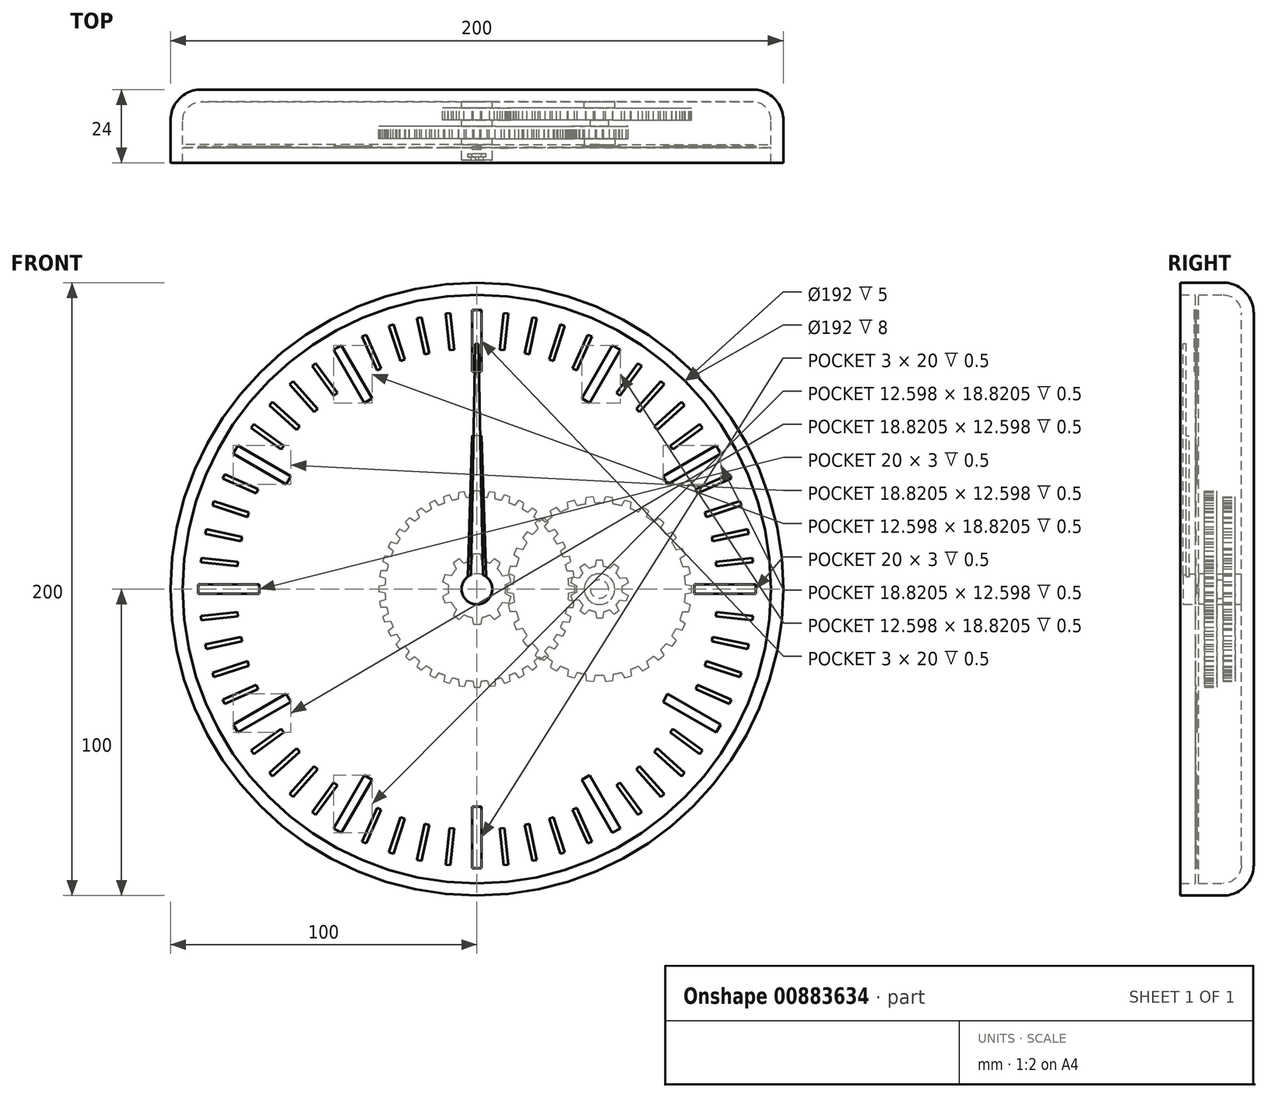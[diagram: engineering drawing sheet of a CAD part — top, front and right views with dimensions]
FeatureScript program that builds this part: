
annotation { "Feature Type Name" : "Feature", "Feature Type Description" : "" }
export const myFeature = defineFeature(function(context is Context, id is Id, definition is map)
    precondition{}
    {
        {
            var Q0;
            Q0=qCreatedBy(makeId("Front.planeOp"),FACE);
            var sketch = newSketch(context, id + "F0", { "sketchPlane" : qUnion([Q0])});
            skCircle(sketch, "E0", {"center": v(0, 0) * mm, "radius": 100 * mm});
            skSolve(sketch);
        }
        {
            var Q0;
            Q0=makeQuery(id+"F0.imprint","IMPRINT",FACE,{"disambiguationData":[TD([[makeQuery(id+"F0.imprint","IMPRINT",EDGE,{"derivedFrom":sQuery(id+"F0.wireOp",EDGE,"E0")}),1.0]])]});
            extrude(context, id + "F1", {"entities" : qUnion([Q0]), "depth" : 24 * mm, "offsetDistance" : 25 * mm});
        }
        {
            var Q0;
            Q0=makeQuery(id+"F1.opExtrude","CAP_EDGE",EDGE,{"disambiguationData":[OSD([sQuery(id+"F0.wireOp",EDGE,"E0")])],"isStart":true});
            fillet(context, id + "F2", {"entities" : qUnion([Q0]), "radius" : 10 * mm, "tangentPropagation" : true, "allowEdgeOverflow" : false});
        }
        {
            var Q0;
            Q0=makeQuery(id+"F1.opExtrude","CAP_FACE",FACE,{"disambiguationData":[OSD([sQuery(id+"F0.wireOp",EDGE,"E0")])],"isStart":false});
            shell(context, id + "F3", {"entities" : qUnion([Q0]), "thickness" : 4 * mm});
        }
        {
            var Q0;
            {var subQ0=sQuery(id+"F0.wireOp",EDGE,"E0");Q0=makeQuery(id+"F3.opShell","OFFSET_FACE",FACE,{"disambiguationData":[OSD([subQ0]),TDD([makeQuery(id+"F1.opExtrude","CAP_FACE",FACE,{"disambiguationData":[OSD([subQ0])],"isStart":true})])]});}
            var sketch = newSketch(context, id + "F4", { "sketchPlane" : qUnion([Q0])});
            skCircle(sketch, "E1", {"center": v(0, 0) * mm, "radius": 3 * mm});
            skCircle(sketch, "E2", {"center": v(0, 0) * mm, "radius": 5 * mm});
            skCircle(sketch, "E3", {"center": v(40, 0) * mm, "radius": 3 * mm});
            skCircle(sketch, "E4", {"center": v(40, 0) * mm, "radius": 5 * mm});
            skSolve(sketch);
        }
        {
            var Q0;
            Q0=makeQuery(id+"F4.imprint","IMPRINT",FACE,{"disambiguationData":[TD([[makeQuery(id+"F4.imprint","IMPRINT",EDGE,{"derivedFrom":sQuery(id+"F4.wireOp",EDGE,"E1")}),-1.0]])]});
            var Q1;
            Q1=makeQuery(id+"F4.imprint","IMPRINT",FACE,{"disambiguationData":[TD([[makeQuery(id+"F4.imprint","IMPRINT",EDGE,{"derivedFrom":sQuery(id+"F4.wireOp",EDGE,"E3")}),-1.0]])]});
            extrude(context, id + "F5", {"entities" : qUnion([Q0, Q1]), "operationType" : NewBodyOperationType.ADD, "depth" : 2 * mm, "offsetDistance" : 25 * mm});
        }
        {
            var Q0;
            Q0=makeQuery(id+"F4.imprint","IMPRINT",FACE,{"disambiguationData":[TD([[makeQuery(id+"F4.imprint","IMPRINT",EDGE,{"derivedFrom":sQuery(id+"F4.wireOp",EDGE,"E1")}),1.0]])]});
            extrude(context, id + "F6", {"entities" : qUnion([Q0]), "depth" : 19 * mm, "offsetDistance" : 25 * mm});
        }
        {
            var Q0;
            Q0=makeQuery(id+"F4.imprint","IMPRINT",FACE,{"disambiguationData":[TD([[makeQuery(id+"F4.imprint","IMPRINT",EDGE,{"derivedFrom":sQuery(id+"F4.wireOp",EDGE,"E3")}),1.0]])]});
            extrude(context, id + "F7", {"entities" : qUnion([Q0]), "depth" : 8 * mm, "offsetDistance" : 25 * mm});
        }
        {
            var Q0;
            Q0=makeQuery(id+"F5.opExtrude","CAP_FACE",FACE,{"disambiguationData":[OSD([sQuery(id+"F4.wireOp",EDGE,"E1"),sQuery(id+"F4.wireOp",EDGE,"E2")])],"isStart":false});
            var sketch = newSketch(context, id + "F8", { "sketchPlane" : qUnion([Q0])});
            skCircle(sketch, "E5", {"center": v(0, 0) * mm, "radius": 9.38 * mm});
            skLineSegment(sketch, "E6", {"start": v(1.55, 9.25) * mm, "end": v(1.18, 11.38) * mm});
            skLineSegment(sketch, "E7", {"start": v(1.18, 11.38) * mm, "end": v(0, 11.38) * mm});
            skLineSegment(sketch, "E8.MirrorCS", {"start": v(-1.18, 11.38) * mm, "end": v(0, 11.38) * mm});
            skLineSegment(sketch, "E9.MirrorCS", {"start": v(-1.55, 9.25) * mm, "end": v(-1.18, 11.38) * mm});
            skLineSegment(sketch, "E10.1.0", {"start": v(-6.7, 6.57) * mm, "end": v(-7.64, 8.51) * mm});
            skLineSegment(sketch, "E10.1.1", {"start": v(-7.64, 8.51) * mm, "end": v(-6.69, 9.2) * mm});
            skLineSegment(sketch, "E10.1.2", {"start": v(-5.73, 9.9) * mm, "end": v(-6.69, 9.2) * mm});
            skLineSegment(sketch, "E10.1.3", {"start": v(-4.18, 8.4) * mm, "end": v(-5.73, 9.9) * mm});
            skLineSegment(sketch, "E10.2.0", {"start": v(-9.27, 1.38) * mm, "end": v(-11.18, 2.4) * mm});
            skLineSegment(sketch, "E10.2.1", {"start": v(-11.18, 2.4) * mm, "end": v(-10.82, 3.52) * mm});
            skLineSegment(sketch, "E10.2.2", {"start": v(-10.45, 4.64) * mm, "end": v(-10.82, 3.52) * mm});
            skLineSegment(sketch, "E10.2.3", {"start": v(-8.31, 4.33) * mm, "end": v(-10.45, 4.64) * mm});
            skLineSegment(sketch, "E10.3.0", {"start": v(-8.31, -4.33) * mm, "end": v(-10.45, -4.64) * mm});
            skLineSegment(sketch, "E10.3.1", {"start": v(-10.45, -4.64) * mm, "end": v(-10.82, -3.52) * mm});
            skLineSegment(sketch, "E10.3.2", {"start": v(-11.18, -2.4) * mm, "end": v(-10.82, -3.52) * mm});
            skLineSegment(sketch, "E10.3.3", {"start": v(-9.27, -1.38) * mm, "end": v(-11.18, -2.4) * mm});
            skLineSegment(sketch, "E10.4.0", {"start": v(-4.18, -8.4) * mm, "end": v(-5.73, -9.9) * mm});
            skLineSegment(sketch, "E10.4.1", {"start": v(-5.73, -9.9) * mm, "end": v(-6.69, -9.2) * mm});
            skLineSegment(sketch, "E10.4.2", {"start": v(-7.64, -8.51) * mm, "end": v(-6.69, -9.2) * mm});
            skLineSegment(sketch, "E10.4.3", {"start": v(-6.7, -6.57) * mm, "end": v(-7.64, -8.51) * mm});
            skLineSegment(sketch, "E10.5.0", {"start": v(1.55, -9.25) * mm, "end": v(1.18, -11.38) * mm});
            skLineSegment(sketch, "E10.5.1", {"start": v(1.18, -11.38) * mm, "end": v(0, -11.38) * mm});
            skLineSegment(sketch, "E10.5.2", {"start": v(-1.18, -11.38) * mm, "end": v(0, -11.38) * mm});
            skLineSegment(sketch, "E10.5.3", {"start": v(-1.55, -9.25) * mm, "end": v(-1.18, -11.38) * mm});
            skLineSegment(sketch, "E10.6.0", {"start": v(6.7, -6.57) * mm, "end": v(7.64, -8.51) * mm});
            skLineSegment(sketch, "E10.6.1", {"start": v(7.64, -8.51) * mm, "end": v(6.69, -9.2) * mm});
            skLineSegment(sketch, "E10.6.2", {"start": v(5.73, -9.9) * mm, "end": v(6.69, -9.2) * mm});
            skLineSegment(sketch, "E10.6.3", {"start": v(4.18, -8.4) * mm, "end": v(5.73, -9.9) * mm});
            skLineSegment(sketch, "E10.7.0", {"start": v(9.27, -1.38) * mm, "end": v(11.18, -2.4) * mm});
            skLineSegment(sketch, "E10.7.1", {"start": v(11.18, -2.4) * mm, "end": v(10.82, -3.52) * mm});
            skLineSegment(sketch, "E10.7.2", {"start": v(10.45, -4.64) * mm, "end": v(10.82, -3.52) * mm});
            skLineSegment(sketch, "E10.7.3", {"start": v(8.31, -4.33) * mm, "end": v(10.45, -4.64) * mm});
            skLineSegment(sketch, "E10.8.0", {"start": v(8.31, 4.33) * mm, "end": v(10.45, 4.64) * mm});
            skLineSegment(sketch, "E10.8.1", {"start": v(10.45, 4.64) * mm, "end": v(10.82, 3.52) * mm});
            skLineSegment(sketch, "E10.8.2", {"start": v(11.18, 2.4) * mm, "end": v(10.82, 3.52) * mm});
            skLineSegment(sketch, "E10.8.3", {"start": v(9.27, 1.38) * mm, "end": v(11.18, 2.4) * mm});
            skLineSegment(sketch, "E10.9.0", {"start": v(4.18, 8.4) * mm, "end": v(5.73, 9.9) * mm});
            skLineSegment(sketch, "E10.9.1", {"start": v(5.73, 9.9) * mm, "end": v(6.69, 9.2) * mm});
            skLineSegment(sketch, "E10.9.2", {"start": v(7.64, 8.51) * mm, "end": v(6.69, 9.2) * mm});
            skLineSegment(sketch, "E10.9.3", {"start": v(6.7, 6.57) * mm, "end": v(7.64, 8.51) * mm});
            skSolve(sketch);
        }
        {
            var Q0;
            Q0 = qSketchRegion(id + "F8", true);
            extrude(context, id + "F9", {"entities" : qUnion([Q0]), "operationType" : NewBodyOperationType.ADD, "depth" : 4 * mm, "offsetDistance" : 25 * mm});
        }
        {
            var Q0;
            Q0=makeQuery(id+"F5.opExtrude","CAP_FACE",FACE,{"disambiguationData":[OSD([sQuery(id+"F4.wireOp",EDGE,"E3"),sQuery(id+"F4.wireOp",EDGE,"E4")])],"isStart":false});
            var sketch = newSketch(context, id + "F10", { "sketchPlane" : qUnion([Q0])});
            skCircle(sketch, "E11", {"center": v(40, 0) * mm, "radius": 28.12 * mm});
            skLineSegment(sketch, "E12", {"start": v(11.92, 1.54) * mm, "end": v(9.88, 1.18) * mm});
            skLineSegment(sketch, "E13", {"start": v(9.88, 1.18) * mm, "end": v(9.88, 0) * mm});
            skLineSegment(sketch, "E14.MirrorCS", {"start": v(9.88, -1.18) * mm, "end": v(9.88, 0) * mm});
            skLineSegment(sketch, "E15.MirrorCS", {"start": v(11.92, -1.54) * mm, "end": v(9.88, -1.18) * mm});
            skLineSegment(sketch, "E16.1.0", {"start": v(12.85, -7.34) * mm, "end": v(10.78, -7.42) * mm});
            skLineSegment(sketch, "E16.1.1", {"start": v(10.78, -7.42) * mm, "end": v(10.53, -6.26) * mm});
            skLineSegment(sketch, "E16.1.2", {"start": v(10.29, -5.11) * mm, "end": v(10.53, -6.26) * mm});
            skLineSegment(sketch, "E16.1.3", {"start": v(12.21, -4.33) * mm, "end": v(10.29, -5.11) * mm});
            skLineSegment(sketch, "E16.2.0", {"start": v(14.97, -12.83) * mm, "end": v(12.96, -13.33) * mm});
            skLineSegment(sketch, "E16.2.1", {"start": v(12.96, -13.33) * mm, "end": v(12.48, -12.25) * mm});
            skLineSegment(sketch, "E16.2.2", {"start": v(12, -11.18) * mm, "end": v(12.48, -12.25) * mm});
            skLineSegment(sketch, "E16.2.3", {"start": v(13.72, -10.02) * mm, "end": v(12, -11.18) * mm});
            skLineSegment(sketch, "E16.3.0", {"start": v(18.18, -17.75) * mm, "end": v(16.32, -18.66) * mm});
            skLineSegment(sketch, "E16.3.1", {"start": v(16.32, -18.66) * mm, "end": v(15.63, -17.7) * mm});
            skLineSegment(sketch, "E16.3.2", {"start": v(14.94, -16.75) * mm, "end": v(15.63, -17.7) * mm});
            skLineSegment(sketch, "E16.3.3", {"start": v(16.38, -15.26) * mm, "end": v(14.94, -16.75) * mm});
            skLineSegment(sketch, "E16.4.0", {"start": v(22.35, -21.9) * mm, "end": v(20.72, -23.18) * mm});
            skLineSegment(sketch, "E16.4.1", {"start": v(20.72, -23.18) * mm, "end": v(19.84, -22.39) * mm});
            skLineSegment(sketch, "E16.4.2", {"start": v(18.97, -21.6) * mm, "end": v(19.84, -22.39) * mm});
            skLineSegment(sketch, "E16.4.3", {"start": v(20.07, -19.84) * mm, "end": v(18.97, -21.6) * mm});
            skLineSegment(sketch, "E16.5.0", {"start": v(27.3, -25.09) * mm, "end": v(25.96, -26.68) * mm});
            skLineSegment(sketch, "E16.5.1", {"start": v(25.96, -26.68) * mm, "end": v(24.94, -26.09) * mm});
            skLineSegment(sketch, "E16.5.2", {"start": v(23.92, -25.5) * mm, "end": v(24.94, -26.09) * mm});
            skLineSegment(sketch, "E16.5.3", {"start": v(24.63, -23.55) * mm, "end": v(23.92, -25.5) * mm});
            skLineSegment(sketch, "E16.6.0", {"start": v(32.78, -27.18) * mm, "end": v(31.81, -29.01) * mm});
            skLineSegment(sketch, "E16.6.1", {"start": v(31.81, -29.01) * mm, "end": v(30.7, -28.65) * mm});
            skLineSegment(sketch, "E16.6.2", {"start": v(29.57, -28.29) * mm, "end": v(30.7, -28.65) * mm});
            skLineSegment(sketch, "E16.6.3", {"start": v(29.86, -26.23) * mm, "end": v(29.57, -28.29) * mm});
            skLineSegment(sketch, "E16.7.0", {"start": v(38.6, -28.09) * mm, "end": v(38.02, -30.08) * mm});
            skLineSegment(sketch, "E16.7.1", {"start": v(38.02, -30.08) * mm, "end": v(36.85, -29.96) * mm});
            skLineSegment(sketch, "E16.7.2", {"start": v(35.68, -29.84) * mm, "end": v(36.85, -29.96) * mm});
            skLineSegment(sketch, "E16.7.3", {"start": v(35.53, -27.77) * mm, "end": v(35.68, -29.84) * mm});
            skLineSegment(sketch, "E16.8.0", {"start": v(44.47, -27.77) * mm, "end": v(44.32, -29.84) * mm});
            skLineSegment(sketch, "E16.8.1", {"start": v(44.32, -29.84) * mm, "end": v(43.15, -29.96) * mm});
            skLineSegment(sketch, "E16.8.2", {"start": v(41.98, -30.08) * mm, "end": v(43.15, -29.96) * mm});
            skLineSegment(sketch, "E16.8.3", {"start": v(41.4, -28.09) * mm, "end": v(41.98, -30.08) * mm});
            skLineSegment(sketch, "E16.9.0", {"start": v(50.14, -26.23) * mm, "end": v(50.43, -28.29) * mm});
            skLineSegment(sketch, "E16.9.1", {"start": v(50.43, -28.29) * mm, "end": v(49.3, -28.65) * mm});
            skLineSegment(sketch, "E16.9.2", {"start": v(48.19, -29.01) * mm, "end": v(49.3, -28.65) * mm});
            skLineSegment(sketch, "E16.9.3", {"start": v(47.22, -27.18) * mm, "end": v(48.19, -29.01) * mm});
            skLineSegment(sketch, "E16.10.0", {"start": v(55.37, -23.55) * mm, "end": v(56.08, -25.5) * mm});
            skLineSegment(sketch, "E16.10.1", {"start": v(56.08, -25.5) * mm, "end": v(55.06, -26.09) * mm});
            skLineSegment(sketch, "E16.10.2", {"start": v(54.04, -26.68) * mm, "end": v(55.06, -26.09) * mm});
            skLineSegment(sketch, "E16.10.3", {"start": v(52.7, -25.09) * mm, "end": v(54.04, -26.68) * mm});
            skLineSegment(sketch, "E16.11.0", {"start": v(59.93, -19.84) * mm, "end": v(61.03, -21.6) * mm});
            skLineSegment(sketch, "E16.11.1", {"start": v(61.03, -21.6) * mm, "end": v(60.16, -22.39) * mm});
            skLineSegment(sketch, "E16.11.2", {"start": v(59.28, -23.18) * mm, "end": v(60.16, -22.39) * mm});
            skLineSegment(sketch, "E16.11.3", {"start": v(57.65, -21.9) * mm, "end": v(59.28, -23.18) * mm});
            skLineSegment(sketch, "E16.12.0", {"start": v(63.62, -15.26) * mm, "end": v(65.06, -16.75) * mm});
            skLineSegment(sketch, "E16.12.1", {"start": v(65.06, -16.75) * mm, "end": v(64.37, -17.7) * mm});
            skLineSegment(sketch, "E16.12.2", {"start": v(63.68, -18.66) * mm, "end": v(64.37, -17.7) * mm});
            skLineSegment(sketch, "E16.12.3", {"start": v(61.82, -17.75) * mm, "end": v(63.68, -18.66) * mm});
            skLineSegment(sketch, "E16.13.0", {"start": v(66.28, -10.02) * mm, "end": v(68, -11.18) * mm});
            skLineSegment(sketch, "E16.13.1", {"start": v(68, -11.18) * mm, "end": v(67.52, -12.25) * mm});
            skLineSegment(sketch, "E16.13.2", {"start": v(67.04, -13.33) * mm, "end": v(67.52, -12.25) * mm});
            skLineSegment(sketch, "E16.13.3", {"start": v(65.03, -12.83) * mm, "end": v(67.04, -13.33) * mm});
            skLineSegment(sketch, "E16.14.0", {"start": v(67.79, -4.33) * mm, "end": v(69.71, -5.11) * mm});
            skLineSegment(sketch, "E16.14.1", {"start": v(69.71, -5.11) * mm, "end": v(69.47, -6.26) * mm});
            skLineSegment(sketch, "E16.14.2", {"start": v(69.22, -7.42) * mm, "end": v(69.47, -6.26) * mm});
            skLineSegment(sketch, "E16.14.3", {"start": v(67.15, -7.34) * mm, "end": v(69.22, -7.42) * mm});
            skLineSegment(sketch, "E16.15.0", {"start": v(68.08, 1.54) * mm, "end": v(70.12, 1.18) * mm});
            skLineSegment(sketch, "E16.15.1", {"start": v(70.12, 1.18) * mm, "end": v(70.12, 0) * mm});
            skLineSegment(sketch, "E16.15.2", {"start": v(70.12, -1.18) * mm, "end": v(70.12, 0) * mm});
            skLineSegment(sketch, "E16.15.3", {"start": v(68.08, -1.54) * mm, "end": v(70.12, -1.18) * mm});
            skLineSegment(sketch, "E16.16.0", {"start": v(67.15, 7.34) * mm, "end": v(69.22, 7.42) * mm});
            skLineSegment(sketch, "E16.16.1", {"start": v(69.22, 7.42) * mm, "end": v(69.47, 6.26) * mm});
            skLineSegment(sketch, "E16.16.2", {"start": v(69.71, 5.11) * mm, "end": v(69.47, 6.26) * mm});
            skLineSegment(sketch, "E16.16.3", {"start": v(67.79, 4.33) * mm, "end": v(69.71, 5.11) * mm});
            skLineSegment(sketch, "E16.17.0", {"start": v(65.03, 12.83) * mm, "end": v(67.04, 13.33) * mm});
            skLineSegment(sketch, "E16.17.1", {"start": v(67.04, 13.33) * mm, "end": v(67.52, 12.25) * mm});
            skLineSegment(sketch, "E16.17.2", {"start": v(68, 11.18) * mm, "end": v(67.52, 12.25) * mm});
            skLineSegment(sketch, "E16.17.3", {"start": v(66.28, 10.02) * mm, "end": v(68, 11.18) * mm});
            skLineSegment(sketch, "E16.18.0", {"start": v(61.82, 17.75) * mm, "end": v(63.68, 18.66) * mm});
            skLineSegment(sketch, "E16.18.1", {"start": v(63.68, 18.66) * mm, "end": v(64.37, 17.7) * mm});
            skLineSegment(sketch, "E16.18.2", {"start": v(65.06, 16.75) * mm, "end": v(64.37, 17.7) * mm});
            skLineSegment(sketch, "E16.18.3", {"start": v(63.62, 15.26) * mm, "end": v(65.06, 16.75) * mm});
            skLineSegment(sketch, "E16.19.0", {"start": v(57.65, 21.9) * mm, "end": v(59.28, 23.18) * mm});
            skLineSegment(sketch, "E16.19.1", {"start": v(59.28, 23.18) * mm, "end": v(60.16, 22.39) * mm});
            skLineSegment(sketch, "E16.19.2", {"start": v(61.03, 21.6) * mm, "end": v(60.16, 22.39) * mm});
            skLineSegment(sketch, "E16.19.3", {"start": v(59.93, 19.84) * mm, "end": v(61.03, 21.6) * mm});
            skLineSegment(sketch, "E16.20.0", {"start": v(52.7, 25.09) * mm, "end": v(54.04, 26.68) * mm});
            skLineSegment(sketch, "E16.20.1", {"start": v(54.04, 26.68) * mm, "end": v(55.06, 26.09) * mm});
            skLineSegment(sketch, "E16.20.2", {"start": v(56.08, 25.5) * mm, "end": v(55.06, 26.09) * mm});
            skLineSegment(sketch, "E16.20.3", {"start": v(55.37, 23.55) * mm, "end": v(56.08, 25.5) * mm});
            skLineSegment(sketch, "E16.21.0", {"start": v(47.22, 27.18) * mm, "end": v(48.19, 29.01) * mm});
            skLineSegment(sketch, "E16.21.1", {"start": v(48.19, 29.01) * mm, "end": v(49.3, 28.65) * mm});
            skLineSegment(sketch, "E16.21.2", {"start": v(50.43, 28.29) * mm, "end": v(49.3, 28.65) * mm});
            skLineSegment(sketch, "E16.21.3", {"start": v(50.14, 26.23) * mm, "end": v(50.43, 28.29) * mm});
            skLineSegment(sketch, "E16.22.0", {"start": v(41.4, 28.09) * mm, "end": v(41.98, 30.08) * mm});
            skLineSegment(sketch, "E16.22.1", {"start": v(41.98, 30.08) * mm, "end": v(43.15, 29.96) * mm});
            skLineSegment(sketch, "E16.22.2", {"start": v(44.32, 29.84) * mm, "end": v(43.15, 29.96) * mm});
            skLineSegment(sketch, "E16.22.3", {"start": v(44.47, 27.77) * mm, "end": v(44.32, 29.84) * mm});
            skLineSegment(sketch, "E16.23.0", {"start": v(35.53, 27.77) * mm, "end": v(35.68, 29.84) * mm});
            skLineSegment(sketch, "E16.23.1", {"start": v(35.68, 29.84) * mm, "end": v(36.85, 29.96) * mm});
            skLineSegment(sketch, "E16.23.2", {"start": v(38.02, 30.08) * mm, "end": v(36.85, 29.96) * mm});
            skLineSegment(sketch, "E16.23.3", {"start": v(38.6, 28.09) * mm, "end": v(38.02, 30.08) * mm});
            skLineSegment(sketch, "E16.24.0", {"start": v(29.86, 26.23) * mm, "end": v(29.57, 28.29) * mm});
            skLineSegment(sketch, "E16.24.1", {"start": v(29.57, 28.29) * mm, "end": v(30.7, 28.65) * mm});
            skLineSegment(sketch, "E16.24.2", {"start": v(31.81, 29.01) * mm, "end": v(30.7, 28.65) * mm});
            skLineSegment(sketch, "E16.24.3", {"start": v(32.78, 27.18) * mm, "end": v(31.81, 29.01) * mm});
            skLineSegment(sketch, "E16.25.0", {"start": v(24.63, 23.55) * mm, "end": v(23.92, 25.5) * mm});
            skLineSegment(sketch, "E16.25.1", {"start": v(23.92, 25.5) * mm, "end": v(24.94, 26.09) * mm});
            skLineSegment(sketch, "E16.25.2", {"start": v(25.96, 26.68) * mm, "end": v(24.94, 26.09) * mm});
            skLineSegment(sketch, "E16.25.3", {"start": v(27.3, 25.09) * mm, "end": v(25.96, 26.68) * mm});
            skLineSegment(sketch, "E16.26.0", {"start": v(20.07, 19.84) * mm, "end": v(18.97, 21.6) * mm});
            skLineSegment(sketch, "E16.26.1", {"start": v(18.97, 21.6) * mm, "end": v(19.84, 22.39) * mm});
            skLineSegment(sketch, "E16.26.2", {"start": v(20.72, 23.18) * mm, "end": v(19.84, 22.39) * mm});
            skLineSegment(sketch, "E16.26.3", {"start": v(22.35, 21.9) * mm, "end": v(20.72, 23.18) * mm});
            skLineSegment(sketch, "E16.27.0", {"start": v(16.38, 15.26) * mm, "end": v(14.94, 16.75) * mm});
            skLineSegment(sketch, "E16.27.1", {"start": v(14.94, 16.75) * mm, "end": v(15.63, 17.7) * mm});
            skLineSegment(sketch, "E16.27.2", {"start": v(16.32, 18.66) * mm, "end": v(15.63, 17.7) * mm});
            skLineSegment(sketch, "E16.27.3", {"start": v(18.18, 17.75) * mm, "end": v(16.32, 18.66) * mm});
            skLineSegment(sketch, "E16.28.0", {"start": v(13.72, 10.02) * mm, "end": v(12, 11.18) * mm});
            skLineSegment(sketch, "E16.28.1", {"start": v(12, 11.18) * mm, "end": v(12.48, 12.25) * mm});
            skLineSegment(sketch, "E16.28.2", {"start": v(12.96, 13.33) * mm, "end": v(12.48, 12.25) * mm});
            skLineSegment(sketch, "E16.28.3", {"start": v(14.97, 12.83) * mm, "end": v(12.96, 13.33) * mm});
            skLineSegment(sketch, "E16.29.0", {"start": v(12.21, 4.33) * mm, "end": v(10.29, 5.11) * mm});
            skLineSegment(sketch, "E16.29.1", {"start": v(10.29, 5.11) * mm, "end": v(10.53, 6.26) * mm});
            skLineSegment(sketch, "E16.29.2", {"start": v(10.78, 7.42) * mm, "end": v(10.53, 6.26) * mm});
            skLineSegment(sketch, "E16.29.3", {"start": v(12.85, 7.34) * mm, "end": v(10.78, 7.42) * mm});
            skSolve(sketch);
        }
        {
            var Q0;
            Q0 = qSketchRegion(id + "F10", true);
            extrude(context, id + "F11", {"entities" : qUnion([Q0]), "operationType" : NewBodyOperationType.ADD, "depth" : 4 * mm, "offsetDistance" : 25 * mm});
        }
        {
            var Q0;
            Q0=makeQuery(id+"F9.opExtrude","CAP_FACE",FACE,{"disambiguationData":[OSD([sQuery(id+"F8.wireOp",EDGE,"E5"),sQuery(id+"F8.wireOp",EDGE,"E6"),sQuery(id+"F8.wireOp",EDGE,"E7"),sQuery(id+"F8.wireOp",EDGE,"E8.MirrorCS"),sQuery(id+"F8.wireOp",EDGE,"E9.MirrorCS"),sQuery(id+"F8.wireOp",EDGE,"E10.1.0"),sQuery(id+"F8.wireOp",EDGE,"E10.1.1"),sQuery(id+"F8.wireOp",EDGE,"E10.1.2"),sQuery(id+"F8.wireOp",EDGE,"E10.1.3"),sQuery(id+"F8.wireOp",EDGE,"E10.2.0"),sQuery(id+"F8.wireOp",EDGE,"E10.2.1"),sQuery(id+"F8.wireOp",EDGE,"E10.2.2"),sQuery(id+"F8.wireOp",EDGE,"E10.2.3"),sQuery(id+"F8.wireOp",EDGE,"E10.3.0"),sQuery(id+"F8.wireOp",EDGE,"E10.3.1"),sQuery(id+"F8.wireOp",EDGE,"E10.3.2"),sQuery(id+"F8.wireOp",EDGE,"E10.3.3"),sQuery(id+"F8.wireOp",EDGE,"E10.4.0"),sQuery(id+"F8.wireOp",EDGE,"E10.4.1"),sQuery(id+"F8.wireOp",EDGE,"E10.4.2"),sQuery(id+"F8.wireOp",EDGE,"E10.4.3"),sQuery(id+"F8.wireOp",EDGE,"E10.5.0"),sQuery(id+"F8.wireOp",EDGE,"E10.5.1"),sQuery(id+"F8.wireOp",EDGE,"E10.5.2"),sQuery(id+"F8.wireOp",EDGE,"E10.5.3"),sQuery(id+"F8.wireOp",EDGE,"E10.6.0"),sQuery(id+"F8.wireOp",EDGE,"E10.6.1"),sQuery(id+"F8.wireOp",EDGE,"E10.6.2"),sQuery(id+"F8.wireOp",EDGE,"E10.6.3"),sQuery(id+"F8.wireOp",EDGE,"E10.7.0"),sQuery(id+"F8.wireOp",EDGE,"E10.7.1"),sQuery(id+"F8.wireOp",EDGE,"E10.7.2"),sQuery(id+"F8.wireOp",EDGE,"E10.7.3"),sQuery(id+"F8.wireOp",EDGE,"E10.8.0"),sQuery(id+"F8.wireOp",EDGE,"E10.8.1"),sQuery(id+"F8.wireOp",EDGE,"E10.8.2"),sQuery(id+"F8.wireOp",EDGE,"E10.8.3"),sQuery(id+"F8.wireOp",EDGE,"E10.9.0"),sQuery(id+"F8.wireOp",EDGE,"E10.9.1"),sQuery(id+"F8.wireOp",EDGE,"E10.9.2"),sQuery(id+"F8.wireOp",EDGE,"E10.9.3")])],"isStart":false});
            var sketch = newSketch(context, id + "F12", { "sketchPlane" : qUnion([Q0])});
            skCircle(sketch, "E17.0", {"center": v(0, 0) * mm, "radius": 5 * mm});
            skCircle(sketch, "E18.0", {"center": v(0, 0) * mm, "radius": 3 * mm});
            skSolve(sketch);
        }
        {
            var Q0;
            Q0 = qSketchRegion(id + "F12", true);
            extrude(context, id + "F13", {"entities" : qUnion([Q0]), "depth" : 2 * mm, "offsetDistance" : 25 * mm});
        }
        {
            var Q0;
            Q0=makeQuery(id+"F13.opExtrude","CAP_FACE",FACE,{"disambiguationData":[OSD([sQuery(id+"F12.wireOp",EDGE,"E17.0"),sQuery(id+"F12.wireOp",EDGE,"E18.0")])],"isStart":false});
            var sketch = newSketch(context, id + "F14", { "sketchPlane" : qUnion([Q0])});
            skCircle(sketch, "E19.0.0", {"center": v(0, 0) * mm, "radius": 3 * mm});
            skCircle(sketch, "E20", {"center": v(0, 0) * mm, "radius": 30 * mm});
            skLineSegment(sketch, "E21", {"start": v(1.3, 29.97) * mm, "end": v(0.94, 32) * mm});
            skLineSegment(sketch, "E22", {"start": v(0.94, 32) * mm, "end": v(0, 32) * mm});
            skLineSegment(sketch, "E23.MirrorCS", {"start": v(-0.94, 32) * mm, "end": v(0, 32) * mm});
            skLineSegment(sketch, "E24.MirrorCS", {"start": v(-1.3, 29.97) * mm, "end": v(-0.94, 32) * mm});
            skLineSegment(sketch, "E25.1.0", {"start": v(-5.97, 29.4) * mm, "end": v(-5.94, 31.46) * mm});
            skLineSegment(sketch, "E25.1.1", {"start": v(-5.94, 31.46) * mm, "end": v(-5, 31.6) * mm});
            skLineSegment(sketch, "E25.1.2", {"start": v(-4.08, 31.75) * mm, "end": v(-5, 31.6) * mm});
            skLineSegment(sketch, "E25.1.3", {"start": v(-3.4, 29.8) * mm, "end": v(-4.08, 31.75) * mm});
            skLineSegment(sketch, "E25.2.0", {"start": v(-10.5, 28.1) * mm, "end": v(-10.78, 30.14) * mm});
            skLineSegment(sketch, "E25.2.1", {"start": v(-10.78, 30.14) * mm, "end": v(-9.89, 30.43) * mm});
            skLineSegment(sketch, "E25.2.2", {"start": v(-9, 30.73) * mm, "end": v(-9.89, 30.43) * mm});
            skLineSegment(sketch, "E25.2.3", {"start": v(-8.03, 28.9) * mm, "end": v(-9, 30.73) * mm});
            skLineSegment(sketch, "E25.3.0", {"start": v(-14.77, 26.11) * mm, "end": v(-15.37, 28.08) * mm});
            skLineSegment(sketch, "E25.3.1", {"start": v(-15.37, 28.08) * mm, "end": v(-14.53, 28.51) * mm});
            skLineSegment(sketch, "E25.3.2", {"start": v(-13.69, 28.94) * mm, "end": v(-14.53, 28.51) * mm});
            skLineSegment(sketch, "E25.3.3", {"start": v(-12.45, 27.3) * mm, "end": v(-13.69, 28.94) * mm});
            skLineSegment(sketch, "E25.4.0", {"start": v(-18.67, 23.48) * mm, "end": v(-19.57, 25.33) * mm});
            skLineSegment(sketch, "E25.4.1", {"start": v(-19.57, 25.33) * mm, "end": v(-18.8, 25.89) * mm});
            skLineSegment(sketch, "E25.4.2", {"start": v(-18.05, 26.44) * mm, "end": v(-18.8, 25.89) * mm});
            skLineSegment(sketch, "E25.4.3", {"start": v(-16.57, 25.01) * mm, "end": v(-18.05, 26.44) * mm});
            skLineSegment(sketch, "E25.5.0", {"start": v(-22.11, 20.27) * mm, "end": v(-23.3, 21.96) * mm});
            skLineSegment(sketch, "E25.5.1", {"start": v(-23.3, 21.96) * mm, "end": v(-22.63, 22.63) * mm});
            skLineSegment(sketch, "E25.5.2", {"start": v(-21.96, 23.3) * mm, "end": v(-22.63, 22.63) * mm});
            skLineSegment(sketch, "E25.5.3", {"start": v(-20.27, 22.11) * mm, "end": v(-21.96, 23.3) * mm});
            skLineSegment(sketch, "E25.6.0", {"start": v(-25.01, 16.57) * mm, "end": v(-26.44, 18.05) * mm});
            skLineSegment(sketch, "E25.6.1", {"start": v(-26.44, 18.05) * mm, "end": v(-25.89, 18.8) * mm});
            skLineSegment(sketch, "E25.6.2", {"start": v(-25.33, 19.57) * mm, "end": v(-25.89, 18.8) * mm});
            skLineSegment(sketch, "E25.6.3", {"start": v(-23.48, 18.67) * mm, "end": v(-25.33, 19.57) * mm});
            skLineSegment(sketch, "E25.7.0", {"start": v(-27.3, 12.45) * mm, "end": v(-28.94, 13.69) * mm});
            skLineSegment(sketch, "E25.7.1", {"start": v(-28.94, 13.69) * mm, "end": v(-28.51, 14.53) * mm});
            skLineSegment(sketch, "E25.7.2", {"start": v(-28.08, 15.37) * mm, "end": v(-28.51, 14.53) * mm});
            skLineSegment(sketch, "E25.7.3", {"start": v(-26.11, 14.77) * mm, "end": v(-28.08, 15.37) * mm});
            skLineSegment(sketch, "E25.8.0", {"start": v(-28.9, 8.03) * mm, "end": v(-30.73, 9) * mm});
            skLineSegment(sketch, "E25.8.1", {"start": v(-30.73, 9) * mm, "end": v(-30.43, 9.89) * mm});
            skLineSegment(sketch, "E25.8.2", {"start": v(-30.14, 10.78) * mm, "end": v(-30.43, 9.89) * mm});
            skLineSegment(sketch, "E25.8.3", {"start": v(-28.1, 10.5) * mm, "end": v(-30.14, 10.78) * mm});
            skLineSegment(sketch, "E25.9.0", {"start": v(-29.8, 3.4) * mm, "end": v(-31.75, 4.08) * mm});
            skLineSegment(sketch, "E25.9.1", {"start": v(-31.75, 4.08) * mm, "end": v(-31.6, 5) * mm});
            skLineSegment(sketch, "E25.9.2", {"start": v(-31.46, 5.94) * mm, "end": v(-31.6, 5) * mm});
            skLineSegment(sketch, "E25.9.3", {"start": v(-29.4, 5.97) * mm, "end": v(-31.46, 5.94) * mm});
            skLineSegment(sketch, "E25.10.0", {"start": v(-29.97, -1.3) * mm, "end": v(-32, -0.94) * mm});
            skLineSegment(sketch, "E25.10.1", {"start": v(-32, -0.94) * mm, "end": v(-32, 0) * mm});
            skLineSegment(sketch, "E25.10.2", {"start": v(-32, 0.94) * mm, "end": v(-32, 0) * mm});
            skLineSegment(sketch, "E25.10.3", {"start": v(-29.97, 1.3) * mm, "end": v(-32, 0.94) * mm});
            skLineSegment(sketch, "E25.11.0", {"start": v(-29.4, -5.97) * mm, "end": v(-31.46, -5.94) * mm});
            skLineSegment(sketch, "E25.11.1", {"start": v(-31.46, -5.94) * mm, "end": v(-31.6, -5) * mm});
            skLineSegment(sketch, "E25.11.2", {"start": v(-31.75, -4.08) * mm, "end": v(-31.6, -5) * mm});
            skLineSegment(sketch, "E25.11.3", {"start": v(-29.8, -3.4) * mm, "end": v(-31.75, -4.08) * mm});
            skLineSegment(sketch, "E25.12.0", {"start": v(-28.1, -10.5) * mm, "end": v(-30.14, -10.78) * mm});
            skLineSegment(sketch, "E25.12.1", {"start": v(-30.14, -10.78) * mm, "end": v(-30.43, -9.89) * mm});
            skLineSegment(sketch, "E25.12.2", {"start": v(-30.73, -9) * mm, "end": v(-30.43, -9.89) * mm});
            skLineSegment(sketch, "E25.12.3", {"start": v(-28.9, -8.03) * mm, "end": v(-30.73, -9) * mm});
            skLineSegment(sketch, "E25.13.0", {"start": v(-26.11, -14.77) * mm, "end": v(-28.08, -15.37) * mm});
            skLineSegment(sketch, "E25.13.1", {"start": v(-28.08, -15.37) * mm, "end": v(-28.51, -14.53) * mm});
            skLineSegment(sketch, "E25.13.2", {"start": v(-28.94, -13.69) * mm, "end": v(-28.51, -14.53) * mm});
            skLineSegment(sketch, "E25.13.3", {"start": v(-27.3, -12.45) * mm, "end": v(-28.94, -13.69) * mm});
            skLineSegment(sketch, "E25.14.0", {"start": v(-23.48, -18.67) * mm, "end": v(-25.33, -19.57) * mm});
            skLineSegment(sketch, "E25.14.1", {"start": v(-25.33, -19.57) * mm, "end": v(-25.89, -18.8) * mm});
            skLineSegment(sketch, "E25.14.2", {"start": v(-26.44, -18.05) * mm, "end": v(-25.89, -18.8) * mm});
            skLineSegment(sketch, "E25.14.3", {"start": v(-25.01, -16.57) * mm, "end": v(-26.44, -18.05) * mm});
            skLineSegment(sketch, "E25.15.0", {"start": v(-20.27, -22.11) * mm, "end": v(-21.96, -23.3) * mm});
            skLineSegment(sketch, "E25.15.1", {"start": v(-21.96, -23.3) * mm, "end": v(-22.63, -22.63) * mm});
            skLineSegment(sketch, "E25.15.2", {"start": v(-23.3, -21.96) * mm, "end": v(-22.63, -22.63) * mm});
            skLineSegment(sketch, "E25.15.3", {"start": v(-22.11, -20.27) * mm, "end": v(-23.3, -21.96) * mm});
            skLineSegment(sketch, "E25.16.0", {"start": v(-16.57, -25.01) * mm, "end": v(-18.05, -26.44) * mm});
            skLineSegment(sketch, "E25.16.1", {"start": v(-18.05, -26.44) * mm, "end": v(-18.8, -25.89) * mm});
            skLineSegment(sketch, "E25.16.2", {"start": v(-19.57, -25.33) * mm, "end": v(-18.8, -25.89) * mm});
            skLineSegment(sketch, "E25.16.3", {"start": v(-18.67, -23.48) * mm, "end": v(-19.57, -25.33) * mm});
            skLineSegment(sketch, "E25.17.0", {"start": v(-12.45, -27.3) * mm, "end": v(-13.69, -28.94) * mm});
            skLineSegment(sketch, "E25.17.1", {"start": v(-13.69, -28.94) * mm, "end": v(-14.53, -28.51) * mm});
            skLineSegment(sketch, "E25.17.2", {"start": v(-15.37, -28.08) * mm, "end": v(-14.53, -28.51) * mm});
            skLineSegment(sketch, "E25.17.3", {"start": v(-14.77, -26.11) * mm, "end": v(-15.37, -28.08) * mm});
            skLineSegment(sketch, "E25.18.0", {"start": v(-8.03, -28.9) * mm, "end": v(-9, -30.73) * mm});
            skLineSegment(sketch, "E25.18.1", {"start": v(-9, -30.73) * mm, "end": v(-9.89, -30.43) * mm});
            skLineSegment(sketch, "E25.18.2", {"start": v(-10.78, -30.14) * mm, "end": v(-9.89, -30.43) * mm});
            skLineSegment(sketch, "E25.18.3", {"start": v(-10.5, -28.1) * mm, "end": v(-10.78, -30.14) * mm});
            skLineSegment(sketch, "E25.19.0", {"start": v(-3.4, -29.8) * mm, "end": v(-4.08, -31.75) * mm});
            skLineSegment(sketch, "E25.19.1", {"start": v(-4.08, -31.75) * mm, "end": v(-5, -31.6) * mm});
            skLineSegment(sketch, "E25.19.2", {"start": v(-5.94, -31.46) * mm, "end": v(-5, -31.6) * mm});
            skLineSegment(sketch, "E25.19.3", {"start": v(-5.97, -29.4) * mm, "end": v(-5.94, -31.46) * mm});
            skLineSegment(sketch, "E25.20.0", {"start": v(1.3, -29.97) * mm, "end": v(0.94, -32) * mm});
            skLineSegment(sketch, "E25.20.1", {"start": v(0.94, -32) * mm, "end": v(0, -32) * mm});
            skLineSegment(sketch, "E25.20.2", {"start": v(-0.94, -32) * mm, "end": v(0, -32) * mm});
            skLineSegment(sketch, "E25.20.3", {"start": v(-1.3, -29.97) * mm, "end": v(-0.94, -32) * mm});
            skLineSegment(sketch, "E25.21.0", {"start": v(5.97, -29.4) * mm, "end": v(5.94, -31.46) * mm});
            skLineSegment(sketch, "E25.21.1", {"start": v(5.94, -31.46) * mm, "end": v(5, -31.6) * mm});
            skLineSegment(sketch, "E25.21.2", {"start": v(4.08, -31.75) * mm, "end": v(5, -31.6) * mm});
            skLineSegment(sketch, "E25.21.3", {"start": v(3.4, -29.8) * mm, "end": v(4.08, -31.75) * mm});
            skLineSegment(sketch, "E25.22.0", {"start": v(10.5, -28.1) * mm, "end": v(10.78, -30.14) * mm});
            skLineSegment(sketch, "E25.22.1", {"start": v(10.78, -30.14) * mm, "end": v(9.89, -30.43) * mm});
            skLineSegment(sketch, "E25.22.2", {"start": v(9, -30.73) * mm, "end": v(9.89, -30.43) * mm});
            skLineSegment(sketch, "E25.22.3", {"start": v(8.03, -28.9) * mm, "end": v(9, -30.73) * mm});
            skLineSegment(sketch, "E25.23.0", {"start": v(14.77, -26.11) * mm, "end": v(15.37, -28.08) * mm});
            skLineSegment(sketch, "E25.23.1", {"start": v(15.37, -28.08) * mm, "end": v(14.53, -28.51) * mm});
            skLineSegment(sketch, "E25.23.2", {"start": v(13.69, -28.94) * mm, "end": v(14.53, -28.51) * mm});
            skLineSegment(sketch, "E25.23.3", {"start": v(12.45, -27.3) * mm, "end": v(13.69, -28.94) * mm});
            skLineSegment(sketch, "E25.24.0", {"start": v(18.67, -23.48) * mm, "end": v(19.57, -25.33) * mm});
            skLineSegment(sketch, "E25.24.1", {"start": v(19.57, -25.33) * mm, "end": v(18.8, -25.89) * mm});
            skLineSegment(sketch, "E25.24.2", {"start": v(18.05, -26.44) * mm, "end": v(18.8, -25.89) * mm});
            skLineSegment(sketch, "E25.24.3", {"start": v(16.57, -25.01) * mm, "end": v(18.05, -26.44) * mm});
            skLineSegment(sketch, "E25.25.0", {"start": v(22.11, -20.27) * mm, "end": v(23.3, -21.96) * mm});
            skLineSegment(sketch, "E25.25.1", {"start": v(23.3, -21.96) * mm, "end": v(22.63, -22.63) * mm});
            skLineSegment(sketch, "E25.25.2", {"start": v(21.96, -23.3) * mm, "end": v(22.63, -22.63) * mm});
            skLineSegment(sketch, "E25.25.3", {"start": v(20.27, -22.11) * mm, "end": v(21.96, -23.3) * mm});
            skLineSegment(sketch, "E25.26.0", {"start": v(25.01, -16.57) * mm, "end": v(26.44, -18.05) * mm});
            skLineSegment(sketch, "E25.26.1", {"start": v(26.44, -18.05) * mm, "end": v(25.89, -18.8) * mm});
            skLineSegment(sketch, "E25.26.2", {"start": v(25.33, -19.57) * mm, "end": v(25.89, -18.8) * mm});
            skLineSegment(sketch, "E25.26.3", {"start": v(23.48, -18.67) * mm, "end": v(25.33, -19.57) * mm});
            skLineSegment(sketch, "E25.27.0", {"start": v(27.3, -12.45) * mm, "end": v(28.94, -13.69) * mm});
            skLineSegment(sketch, "E25.27.1", {"start": v(28.94, -13.69) * mm, "end": v(28.51, -14.53) * mm});
            skLineSegment(sketch, "E25.27.2", {"start": v(28.08, -15.37) * mm, "end": v(28.51, -14.53) * mm});
            skLineSegment(sketch, "E25.27.3", {"start": v(26.11, -14.77) * mm, "end": v(28.08, -15.37) * mm});
            skLineSegment(sketch, "E25.28.0", {"start": v(28.9, -8.03) * mm, "end": v(30.73, -9) * mm});
            skLineSegment(sketch, "E25.28.1", {"start": v(30.73, -9) * mm, "end": v(30.43, -9.89) * mm});
            skLineSegment(sketch, "E25.28.2", {"start": v(30.14, -10.78) * mm, "end": v(30.43, -9.89) * mm});
            skLineSegment(sketch, "E25.28.3", {"start": v(28.1, -10.5) * mm, "end": v(30.14, -10.78) * mm});
            skLineSegment(sketch, "E25.29.0", {"start": v(29.8, -3.4) * mm, "end": v(31.75, -4.08) * mm});
            skLineSegment(sketch, "E25.29.1", {"start": v(31.75, -4.08) * mm, "end": v(31.6, -5) * mm});
            skLineSegment(sketch, "E25.29.2", {"start": v(31.46, -5.94) * mm, "end": v(31.6, -5) * mm});
            skLineSegment(sketch, "E25.29.3", {"start": v(29.4, -5.97) * mm, "end": v(31.46, -5.94) * mm});
            skLineSegment(sketch, "E25.30.0", {"start": v(29.97, 1.3) * mm, "end": v(32, 0.94) * mm});
            skLineSegment(sketch, "E25.30.1", {"start": v(32, 0.94) * mm, "end": v(32, 0) * mm});
            skLineSegment(sketch, "E25.30.2", {"start": v(32, -0.94) * mm, "end": v(32, 0) * mm});
            skLineSegment(sketch, "E25.30.3", {"start": v(29.97, -1.3) * mm, "end": v(32, -0.94) * mm});
            skLineSegment(sketch, "E25.31.0", {"start": v(29.4, 5.97) * mm, "end": v(31.46, 5.94) * mm});
            skLineSegment(sketch, "E25.31.1", {"start": v(31.46, 5.94) * mm, "end": v(31.6, 5) * mm});
            skLineSegment(sketch, "E25.31.2", {"start": v(31.75, 4.08) * mm, "end": v(31.6, 5) * mm});
            skLineSegment(sketch, "E25.31.3", {"start": v(29.8, 3.4) * mm, "end": v(31.75, 4.08) * mm});
            skLineSegment(sketch, "E25.32.0", {"start": v(28.1, 10.5) * mm, "end": v(30.14, 10.78) * mm});
            skLineSegment(sketch, "E25.32.1", {"start": v(30.14, 10.78) * mm, "end": v(30.43, 9.89) * mm});
            skLineSegment(sketch, "E25.32.2", {"start": v(30.73, 9) * mm, "end": v(30.43, 9.89) * mm});
            skLineSegment(sketch, "E25.32.3", {"start": v(28.9, 8.03) * mm, "end": v(30.73, 9) * mm});
            skLineSegment(sketch, "E25.33.0", {"start": v(26.11, 14.77) * mm, "end": v(28.08, 15.37) * mm});
            skLineSegment(sketch, "E25.33.1", {"start": v(28.08, 15.37) * mm, "end": v(28.51, 14.53) * mm});
            skLineSegment(sketch, "E25.33.2", {"start": v(28.94, 13.69) * mm, "end": v(28.51, 14.53) * mm});
            skLineSegment(sketch, "E25.33.3", {"start": v(27.3, 12.45) * mm, "end": v(28.94, 13.69) * mm});
            skLineSegment(sketch, "E25.34.0", {"start": v(23.48, 18.67) * mm, "end": v(25.33, 19.57) * mm});
            skLineSegment(sketch, "E25.34.1", {"start": v(25.33, 19.57) * mm, "end": v(25.89, 18.8) * mm});
            skLineSegment(sketch, "E25.34.2", {"start": v(26.44, 18.05) * mm, "end": v(25.89, 18.8) * mm});
            skLineSegment(sketch, "E25.34.3", {"start": v(25.01, 16.57) * mm, "end": v(26.44, 18.05) * mm});
            skLineSegment(sketch, "E25.35.0", {"start": v(20.27, 22.11) * mm, "end": v(21.96, 23.3) * mm});
            skLineSegment(sketch, "E25.35.1", {"start": v(21.96, 23.3) * mm, "end": v(22.63, 22.63) * mm});
            skLineSegment(sketch, "E25.35.2", {"start": v(23.3, 21.96) * mm, "end": v(22.63, 22.63) * mm});
            skLineSegment(sketch, "E25.35.3", {"start": v(22.11, 20.27) * mm, "end": v(23.3, 21.96) * mm});
            skLineSegment(sketch, "E25.36.0", {"start": v(16.57, 25.01) * mm, "end": v(18.05, 26.44) * mm});
            skLineSegment(sketch, "E25.36.1", {"start": v(18.05, 26.44) * mm, "end": v(18.8, 25.89) * mm});
            skLineSegment(sketch, "E25.36.2", {"start": v(19.57, 25.33) * mm, "end": v(18.8, 25.89) * mm});
            skLineSegment(sketch, "E25.36.3", {"start": v(18.67, 23.48) * mm, "end": v(19.57, 25.33) * mm});
            skLineSegment(sketch, "E25.37.0", {"start": v(12.45, 27.3) * mm, "end": v(13.69, 28.94) * mm});
            skLineSegment(sketch, "E25.37.1", {"start": v(13.69, 28.94) * mm, "end": v(14.53, 28.51) * mm});
            skLineSegment(sketch, "E25.37.2", {"start": v(15.37, 28.08) * mm, "end": v(14.53, 28.51) * mm});
            skLineSegment(sketch, "E25.37.3", {"start": v(14.77, 26.11) * mm, "end": v(15.37, 28.08) * mm});
            skLineSegment(sketch, "E25.38.0", {"start": v(8.03, 28.9) * mm, "end": v(9, 30.73) * mm});
            skLineSegment(sketch, "E25.38.1", {"start": v(9, 30.73) * mm, "end": v(9.89, 30.43) * mm});
            skLineSegment(sketch, "E25.38.2", {"start": v(10.78, 30.14) * mm, "end": v(9.89, 30.43) * mm});
            skLineSegment(sketch, "E25.38.3", {"start": v(10.5, 28.1) * mm, "end": v(10.78, 30.14) * mm});
            skLineSegment(sketch, "E25.39.0", {"start": v(3.4, 29.8) * mm, "end": v(4.08, 31.75) * mm});
            skLineSegment(sketch, "E25.39.1", {"start": v(4.08, 31.75) * mm, "end": v(5, 31.6) * mm});
            skLineSegment(sketch, "E25.39.2", {"start": v(5.94, 31.46) * mm, "end": v(5, 31.6) * mm});
            skLineSegment(sketch, "E25.39.3", {"start": v(5.97, 29.4) * mm, "end": v(5.94, 31.46) * mm});
            skSolve(sketch);
        }
        {
            var Q0;
            Q0 = qSketchRegion(id + "F14", true);
            extrude(context, id + "F15", {"entities" : qUnion([Q0]), "operationType" : NewBodyOperationType.ADD, "depth" : 4 * mm, "offsetDistance" : 25 * mm});
        }
        {
            var Q0;
            Q0=makeQuery(id+"F7.opExtrude","CAP_FACE",FACE,{"disambiguationData":[OSD([sQuery(id+"F4.wireOp",EDGE,"E3")])],"isStart":false});
            var sketch = newSketch(context, id + "F16", { "sketchPlane" : qUnion([Q0])});
            skCircle(sketch, "E26", {"center": v(40, 0) * mm, "radius": 7.5 * mm});
            skLineSegment(sketch, "E27", {"start": v(40, 0) * mm, "end": v(40, 7.5) * mm, "construction": true});
            skLineSegment(sketch, "E28", {"start": v(38.68, 7.38) * mm, "end": v(39.06, 9.5) * mm});
            skLineSegment(sketch, "E29", {"start": v(39.06, 9.5) * mm, "end": v(40.94, 9.5) * mm});
            skLineSegment(sketch, "E30.MirrorCS", {"start": v(41.32, 7.38) * mm, "end": v(40.94, 9.5) * mm});
            skLineSegment(sketch, "E31.1.0", {"start": v(34.6, 5.2) * mm, "end": v(33.65, 7.13) * mm});
            skLineSegment(sketch, "E31.1.1", {"start": v(33.65, 7.13) * mm, "end": v(35.18, 8.24) * mm});
            skLineSegment(sketch, "E31.1.2", {"start": v(36.72, 6.75) * mm, "end": v(35.18, 8.24) * mm});
            skLineSegment(sketch, "E31.2.0", {"start": v(32.57, 1.03) * mm, "end": v(30.67, 2.04) * mm});
            skLineSegment(sketch, "E31.2.1", {"start": v(30.67, 2.04) * mm, "end": v(31.26, 3.83) * mm});
            skLineSegment(sketch, "E31.2.2", {"start": v(33.38, 3.53) * mm, "end": v(31.26, 3.83) * mm});
            skLineSegment(sketch, "E32.1.3.0", {"start": v(33.38, -3.53) * mm, "end": v(31.26, -3.83) * mm});
            skLineSegment(sketch, "E32.3.3.0", {"start": v(31.26, -3.83) * mm, "end": v(30.67, -2.04) * mm});
            skLineSegment(sketch, "E32.6.3.0", {"start": v(32.57, -1.03) * mm, "end": v(30.67, -2.04) * mm});
            skLineSegment(sketch, "E32.1.4.0", {"start": v(36.72, -6.75) * mm, "end": v(35.18, -8.24) * mm});
            skLineSegment(sketch, "E32.3.4.0", {"start": v(35.18, -8.24) * mm, "end": v(33.65, -7.13) * mm});
            skLineSegment(sketch, "E32.6.4.0", {"start": v(34.6, -5.2) * mm, "end": v(33.65, -7.13) * mm});
            skLineSegment(sketch, "E32.1.5.0", {"start": v(41.32, -7.38) * mm, "end": v(40.94, -9.5) * mm});
            skLineSegment(sketch, "E32.3.5.0", {"start": v(40.94, -9.5) * mm, "end": v(39.06, -9.5) * mm});
            skLineSegment(sketch, "E32.6.5.0", {"start": v(38.68, -7.38) * mm, "end": v(39.06, -9.5) * mm});
            skLineSegment(sketch, "E32.1.6.0", {"start": v(45.4, -5.2) * mm, "end": v(46.35, -7.13) * mm});
            skLineSegment(sketch, "E32.3.6.0", {"start": v(46.35, -7.13) * mm, "end": v(44.82, -8.24) * mm});
            skLineSegment(sketch, "E32.6.6.0", {"start": v(43.28, -6.75) * mm, "end": v(44.82, -8.24) * mm});
            skLineSegment(sketch, "E32.1.7.0", {"start": v(47.43, -1.03) * mm, "end": v(49.33, -2.04) * mm});
            skLineSegment(sketch, "E32.3.7.0", {"start": v(49.33, -2.04) * mm, "end": v(48.74, -3.83) * mm});
            skLineSegment(sketch, "E32.6.7.0", {"start": v(46.62, -3.53) * mm, "end": v(48.74, -3.83) * mm});
            skLineSegment(sketch, "E32.1.8.0", {"start": v(46.62, 3.53) * mm, "end": v(48.74, 3.83) * mm});
            skLineSegment(sketch, "E32.3.8.0", {"start": v(48.74, 3.83) * mm, "end": v(49.33, 2.04) * mm});
            skLineSegment(sketch, "E32.6.8.0", {"start": v(47.43, 1.03) * mm, "end": v(49.33, 2.04) * mm});
            skLineSegment(sketch, "E32.1.9.0", {"start": v(43.28, 6.75) * mm, "end": v(44.82, 8.24) * mm});
            skLineSegment(sketch, "E32.3.9.0", {"start": v(44.82, 8.24) * mm, "end": v(46.35, 7.13) * mm});
            skLineSegment(sketch, "E32.6.9.0", {"start": v(45.4, 5.2) * mm, "end": v(46.35, 7.13) * mm});
            skSolve(sketch);
        }
        {
            var Q0;
            Q0 = qSketchRegion(id + "F16", true);
            extrude(context, id + "F17", {"entities" : qUnion([Q0]), "operationType" : NewBodyOperationType.ADD, "depth" : 4 * mm, "offsetDistance" : 25 * mm});
        }
        {
            var Q0;
            Q0=makeQuery(id+"F17.opExtrude","CAP_FACE",FACE,{"disambiguationData":[OSD([sQuery(id+"F16.wireOp",EDGE,"E26"),sQuery(id+"F16.wireOp",EDGE,"E28"),sQuery(id+"F16.wireOp",EDGE,"E29"),sQuery(id+"F16.wireOp",EDGE,"E30.MirrorCS"),sQuery(id+"F16.wireOp",EDGE,"E31.1.0"),sQuery(id+"F16.wireOp",EDGE,"E31.1.1"),sQuery(id+"F16.wireOp",EDGE,"E31.1.2"),sQuery(id+"F16.wireOp",EDGE,"E31.2.0"),sQuery(id+"F16.wireOp",EDGE,"E31.2.1"),sQuery(id+"F16.wireOp",EDGE,"E31.2.2"),sQuery(id+"F16.wireOp",EDGE,"E32.1.3.0"),sQuery(id+"F16.wireOp",EDGE,"E32.3.3.0"),sQuery(id+"F16.wireOp",EDGE,"E32.6.3.0"),sQuery(id+"F16.wireOp",EDGE,"E32.1.4.0"),sQuery(id+"F16.wireOp",EDGE,"E32.3.4.0"),sQuery(id+"F16.wireOp",EDGE,"E32.6.4.0"),sQuery(id+"F16.wireOp",EDGE,"E32.1.5.0"),sQuery(id+"F16.wireOp",EDGE,"E32.3.5.0"),sQuery(id+"F16.wireOp",EDGE,"E32.6.5.0"),sQuery(id+"F16.wireOp",EDGE,"E32.1.6.0"),sQuery(id+"F16.wireOp",EDGE,"E32.3.6.0"),sQuery(id+"F16.wireOp",EDGE,"E32.6.6.0"),sQuery(id+"F16.wireOp",EDGE,"E32.1.7.0"),sQuery(id+"F16.wireOp",EDGE,"E32.3.7.0"),sQuery(id+"F16.wireOp",EDGE,"E32.6.7.0"),sQuery(id+"F16.wireOp",EDGE,"E32.1.8.0"),sQuery(id+"F16.wireOp",EDGE,"E32.3.8.0"),sQuery(id+"F16.wireOp",EDGE,"E32.6.8.0"),sQuery(id+"F16.wireOp",EDGE,"E32.1.9.0"),sQuery(id+"F16.wireOp",EDGE,"E32.3.9.0"),sQuery(id+"F16.wireOp",EDGE,"E32.6.9.0")])],"isStart":false});
            var sketch = newSketch(context, id + "F18", { "sketchPlane" : qUnion([Q0])});
            skCircle(sketch, "E33.0", {"center": v(40, 0) * mm, "radius": 3 * mm});
            skSolve(sketch);
        }
        {
            var Q0;
            Q0=makeQuery(id+"F18.imprint","IMPRINT",FACE,{"disambiguationData":[TD([[makeQuery(id+"F18.imprint","IMPRINT",EDGE,{"derivedFrom":sQuery(id+"F18.wireOp",EDGE,"E33.0")}),1.0]])]});
            extrude(context, id + "F19", {"entities" : qUnion([Q0]), "operationType" : NewBodyOperationType.ADD, "depth" : 2 * mm, "offsetDistance" : 25 * mm});
        }
        {
            var Q0;
            Q0=makeQuery(id+"F19.opExtrude","CAP_FACE",FACE,{"disambiguationData":[OSD([sQuery(id+"F18.wireOp",EDGE,"E33.0")])],"isStart":false});
            var sketch = newSketch(context, id + "F20", { "sketchPlane" : qUnion([Q0])});
            skCircle(sketch, "E34", {"center": v(0, 0) * mm, "radius": 98 * mm});
            skCircle(sketch, "E35.0", {"center": v(0, 0) * mm, "radius": 5 * mm});
            skSolve(sketch);
        }
        {
            var Q0;
            Q0 = qSketchRegion(id + "F20", true);
            extrude(context, id + "F21", {"entities" : qUnion([Q0]), "depth" : 1 * mm, "offsetDistance" : 25 * mm});
        }
        {
            var Q0;
            Q0=makeQuery(id+"F21.opExtrude","SWEPT_BODY",BODY,{"disambiguationData":[OSD([sQuery(id+"F20.wireOp",EDGE,"E34"),sQuery(id+"F20.wireOp",EDGE,"E35.0")])]});
            var Q1;
            Q1=makeQuery(id+"F1.opExtrude","SWEPT_BODY",BODY,{"disambiguationData":[OSD([sQuery(id+"F0.wireOp",EDGE,"E0")])]});
            booleanBodies(context, id + "F22", {"operationType" : BooleanOperationType.SUBTRACTION, "tools" : qUnion([Q0]), "targets" : qUnion([Q1]), "keepTools" : true});
        }
        {
            var Q0;
            Q0=makeQuery(id+"F21.opExtrude","CAP_FACE",FACE,{"disambiguationData":[OSD([sQuery(id+"F20.wireOp",EDGE,"E34"),sQuery(id+"F20.wireOp",EDGE,"E35.0")])],"isStart":true});
            var sketch = newSketch(context, id + "F23", { "sketchPlane" : qUnion([Q0])});
            skCircle(sketch, "E36.0.0", {"center": v(-40, 0) * mm, "radius": 5 * mm});
            skCircle(sketch, "E37.0", {"center": v(-40, 0) * mm, "radius": 3 * mm});
            skSolve(sketch);
        }
        {
            var Q0;
            Q0 = qSketchRegion(id + "F23", true);
            extrude(context, id + "F24", {"entities" : qUnion([Q0]), "operationType" : NewBodyOperationType.ADD, "endBound" : BoundingType.UP_TO_NEXT, "depth" : 25 * mm, "offsetDistance" : 25 * mm});
        }
        {
            var Q0;
            Q0=makeQuery(id+"F21.opExtrude","CAP_FACE",FACE,{"disambiguationData":[OSD([sQuery(id+"F20.wireOp",EDGE,"E34"),sQuery(id+"F20.wireOp",EDGE,"E35.0")])],"isStart":false});
            var sketch = newSketch(context, id + "F25", { "sketchPlane" : qUnion([Q0])});
            skLineSegment(sketch, "E38.bottom", {"start": v(-1.5, 91) * mm, "end": v(1.5, 91) * mm});
            skLineSegment(sketch, "E38.top", {"start": v(-1.5, 71) * mm, "end": v(1.5, 71) * mm});
            skLineSegment(sketch, "E38.left", {"start": v(-1.5, 91) * mm, "end": v(-1.5, 71) * mm});
            skLineSegment(sketch, "E38.right", {"start": v(1.5, 91) * mm, "end": v(1.5, 71) * mm});
            skPoint(sketch, "E38.middle", {"position": v(0, 81) * mm});
            skLineSegment(sketch, "E39.1.0", {"start": v(-46.8, 78.06) * mm, "end": v(-36.8, 60.74) * mm});
            skLineSegment(sketch, "E39.1.1", {"start": v(-46.8, 78.06) * mm, "end": v(-44.2, 79.56) * mm});
            skLineSegment(sketch, "E39.1.2", {"start": v(-44.2, 79.56) * mm, "end": v(-34.2, 62.24) * mm});
            skLineSegment(sketch, "E39.1.3", {"start": v(-36.8, 60.74) * mm, "end": v(-34.2, 62.24) * mm});
            skLineSegment(sketch, "E39.2.0", {"start": v(-79.56, 44.2) * mm, "end": v(-62.24, 34.2) * mm});
            skLineSegment(sketch, "E39.2.1", {"start": v(-79.56, 44.2) * mm, "end": v(-78.06, 46.8) * mm});
            skLineSegment(sketch, "E39.2.2", {"start": v(-78.06, 46.8) * mm, "end": v(-60.74, 36.8) * mm});
            skLineSegment(sketch, "E39.2.3", {"start": v(-62.24, 34.2) * mm, "end": v(-60.74, 36.8) * mm});
            skLineSegment(sketch, "E39.3.0", {"start": v(-91, -1.5) * mm, "end": v(-71, -1.5) * mm});
            skLineSegment(sketch, "E39.3.1", {"start": v(-91, -1.5) * mm, "end": v(-91, 1.5) * mm});
            skLineSegment(sketch, "E39.3.2", {"start": v(-91, 1.5) * mm, "end": v(-71, 1.5) * mm});
            skLineSegment(sketch, "E39.3.3", {"start": v(-71, -1.5) * mm, "end": v(-71, 1.5) * mm});
            skLineSegment(sketch, "E39.4.0", {"start": v(-78.06, -46.8) * mm, "end": v(-60.74, -36.8) * mm});
            skLineSegment(sketch, "E39.4.1", {"start": v(-78.06, -46.8) * mm, "end": v(-79.56, -44.2) * mm});
            skLineSegment(sketch, "E39.4.2", {"start": v(-79.56, -44.2) * mm, "end": v(-62.24, -34.2) * mm});
            skLineSegment(sketch, "E39.4.3", {"start": v(-60.74, -36.8) * mm, "end": v(-62.24, -34.2) * mm});
            skLineSegment(sketch, "E39.5.0", {"start": v(-44.2, -79.56) * mm, "end": v(-34.2, -62.24) * mm});
            skLineSegment(sketch, "E39.5.1", {"start": v(-44.2, -79.56) * mm, "end": v(-46.8, -78.06) * mm});
            skLineSegment(sketch, "E39.5.2", {"start": v(-46.8, -78.06) * mm, "end": v(-36.8, -60.74) * mm});
            skLineSegment(sketch, "E39.5.3", {"start": v(-34.2, -62.24) * mm, "end": v(-36.8, -60.74) * mm});
            skLineSegment(sketch, "E39.6.0", {"start": v(1.5, -91) * mm, "end": v(1.5, -71) * mm});
            skLineSegment(sketch, "E39.6.1", {"start": v(1.5, -91) * mm, "end": v(-1.5, -91) * mm});
            skLineSegment(sketch, "E39.6.2", {"start": v(-1.5, -91) * mm, "end": v(-1.5, -71) * mm});
            skLineSegment(sketch, "E39.6.3", {"start": v(1.5, -71) * mm, "end": v(-1.5, -71) * mm});
            skLineSegment(sketch, "E39.7.0", {"start": v(46.8, -78.06) * mm, "end": v(36.8, -60.74) * mm});
            skLineSegment(sketch, "E39.7.1", {"start": v(46.8, -78.06) * mm, "end": v(44.2, -79.56) * mm});
            skLineSegment(sketch, "E39.7.2", {"start": v(44.2, -79.56) * mm, "end": v(34.2, -62.24) * mm});
            skLineSegment(sketch, "E39.7.3", {"start": v(36.8, -60.74) * mm, "end": v(34.2, -62.24) * mm});
            skLineSegment(sketch, "E39.8.0", {"start": v(79.56, -44.2) * mm, "end": v(62.24, -34.2) * mm});
            skLineSegment(sketch, "E39.8.1", {"start": v(79.56, -44.2) * mm, "end": v(78.06, -46.8) * mm});
            skLineSegment(sketch, "E39.8.2", {"start": v(78.06, -46.8) * mm, "end": v(60.74, -36.8) * mm});
            skLineSegment(sketch, "E39.8.3", {"start": v(62.24, -34.2) * mm, "end": v(60.74, -36.8) * mm});
            skLineSegment(sketch, "E39.9.0", {"start": v(91, 1.5) * mm, "end": v(71, 1.5) * mm});
            skLineSegment(sketch, "E39.9.1", {"start": v(91, 1.5) * mm, "end": v(91, -1.5) * mm});
            skLineSegment(sketch, "E39.9.2", {"start": v(91, -1.5) * mm, "end": v(71, -1.5) * mm});
            skLineSegment(sketch, "E39.9.3", {"start": v(71, 1.5) * mm, "end": v(71, -1.5) * mm});
            skLineSegment(sketch, "E39.10.0", {"start": v(78.06, 46.8) * mm, "end": v(60.74, 36.8) * mm});
            skLineSegment(sketch, "E39.10.1", {"start": v(78.06, 46.8) * mm, "end": v(79.56, 44.2) * mm});
            skLineSegment(sketch, "E39.10.2", {"start": v(79.56, 44.2) * mm, "end": v(62.24, 34.2) * mm});
            skLineSegment(sketch, "E39.10.3", {"start": v(60.74, 36.8) * mm, "end": v(62.24, 34.2) * mm});
            skLineSegment(sketch, "E39.11.0", {"start": v(44.2, 79.56) * mm, "end": v(34.2, 62.24) * mm});
            skLineSegment(sketch, "E39.11.1", {"start": v(44.2, 79.56) * mm, "end": v(46.8, 78.06) * mm});
            skLineSegment(sketch, "E39.11.2", {"start": v(46.8, 78.06) * mm, "end": v(36.8, 60.74) * mm});
            skLineSegment(sketch, "E39.11.3", {"start": v(34.2, 62.24) * mm, "end": v(36.8, 60.74) * mm});
            skPoint(sketch, "E39.center", {"position": v(0, 0) * mm});
            skSolve(sketch);
        }
        {
            var Q0;
            Q0 = qSketchRegion(id + "F25", true);
            extrude(context, id + "F26", {"entities" : qUnion([Q0]), "operationType" : NewBodyOperationType.REMOVE, "oppositeDirection" : true, "depth" : 0.5 * mm, "offsetDistance" : 25 * mm});
        }
        {
            var Q0;
            Q0=makeQuery(id+"F21.opExtrude","CAP_FACE",FACE,{"disambiguationData":[OSD([sQuery(id+"F20.wireOp",EDGE,"E34"),sQuery(id+"F20.wireOp",EDGE,"E35.0")])],"isStart":false});
            var sketch = newSketch(context, id + "F27", { "sketchPlane" : qUnion([Q0])});
            skLineSegment(sketch, "E40.bottom", {"start": v(0.75, 90.5) * mm, "end": v(-0.75, 90.5) * mm});
            skLineSegment(sketch, "E40.top", {"start": v(0.75, 78.5) * mm, "end": v(-0.75, 78.5) * mm});
            skLineSegment(sketch, "E40.left", {"start": v(0.75, 90.5) * mm, "end": v(0.75, 78.5) * mm});
            skLineSegment(sketch, "E40.right", {"start": v(-0.75, 90.5) * mm, "end": v(-0.75, 78.5) * mm});
            skPoint(sketch, "E40.middle", {"position": v(0, 84.5) * mm});
            skLineSegment(sketch, "E41.1.0", {"start": v(-8.71, 90.08) * mm, "end": v(-10.2, 89.93) * mm});
            skLineSegment(sketch, "E41.1.1", {"start": v(-7.46, 78.15) * mm, "end": v(-8.95, 78) * mm});
            skLineSegment(sketch, "E41.1.2", {"start": v(-10.2, 89.93) * mm, "end": v(-8.95, 78) * mm});
            skLineSegment(sketch, "E41.1.3", {"start": v(-8.71, 90.08) * mm, "end": v(-7.46, 78.15) * mm});
            skLineSegment(sketch, "E41.2.0", {"start": v(-18.08, 88.68) * mm, "end": v(-19.55, 88.37) * mm});
            skLineSegment(sketch, "E41.2.1", {"start": v(-15.59, 76.94) * mm, "end": v(-17.05, 76.63) * mm});
            skLineSegment(sketch, "E41.2.2", {"start": v(-19.55, 88.37) * mm, "end": v(-17.05, 76.63) * mm});
            skLineSegment(sketch, "E41.2.3", {"start": v(-18.08, 88.68) * mm, "end": v(-15.59, 76.94) * mm});
            skLineSegment(sketch, "E41.3.0", {"start": v(-27.25, 86.3) * mm, "end": v(-28.68, 85.84) * mm});
            skLineSegment(sketch, "E41.3.1", {"start": v(-23.54, 74.89) * mm, "end": v(-24.97, 74.43) * mm});
            skLineSegment(sketch, "E41.3.2", {"start": v(-28.68, 85.84) * mm, "end": v(-24.97, 74.43) * mm});
            skLineSegment(sketch, "E41.3.3", {"start": v(-27.25, 86.3) * mm, "end": v(-23.54, 74.89) * mm});
            skLineSegment(sketch, "E41.4.0", {"start": v(-36.12, 82.98) * mm, "end": v(-37.5, 82.37) * mm});
            skLineSegment(sketch, "E41.4.1", {"start": v(-31.24, 72.02) * mm, "end": v(-32.61, 71.4) * mm});
            skLineSegment(sketch, "E41.4.2", {"start": v(-37.5, 82.37) * mm, "end": v(-32.61, 71.4) * mm});
            skLineSegment(sketch, "E41.4.3", {"start": v(-36.12, 82.98) * mm, "end": v(-31.24, 72.02) * mm});
            skLineSegment(sketch, "E41.5.0", {"start": v(-44.6, 78.75) * mm, "end": v(-45.9, 78) * mm});
            skLineSegment(sketch, "E41.5.1", {"start": v(-38.6, 68.36) * mm, "end": v(-39.9, 67.6) * mm});
            skLineSegment(sketch, "E41.5.2", {"start": v(-45.9, 78) * mm, "end": v(-39.9, 67.6) * mm});
            skLineSegment(sketch, "E41.5.3", {"start": v(-44.6, 78.75) * mm, "end": v(-38.6, 68.36) * mm});
            skLineSegment(sketch, "E41.6.0", {"start": v(-52.59, 73.66) * mm, "end": v(-53.8, 72.78) * mm});
            skLineSegment(sketch, "E41.6.1", {"start": v(-45.53, 63.95) * mm, "end": v(-46.75, 63.07) * mm});
            skLineSegment(sketch, "E41.6.2", {"start": v(-53.8, 72.78) * mm, "end": v(-46.75, 63.07) * mm});
            skLineSegment(sketch, "E41.6.3", {"start": v(-52.59, 73.66) * mm, "end": v(-45.53, 63.95) * mm});
            skLineSegment(sketch, "E41.7.0", {"start": v(-60, 67.76) * mm, "end": v(-61.11, 66.75) * mm});
            skLineSegment(sketch, "E41.7.1", {"start": v(-51.97, 58.84) * mm, "end": v(-53.08, 57.84) * mm});
            skLineSegment(sketch, "E41.7.2", {"start": v(-61.11, 66.75) * mm, "end": v(-53.08, 57.84) * mm});
            skLineSegment(sketch, "E41.7.3", {"start": v(-60, 67.76) * mm, "end": v(-51.97, 58.84) * mm});
            skLineSegment(sketch, "E41.8.0", {"start": v(-66.75, 61.11) * mm, "end": v(-67.76, 60) * mm});
            skLineSegment(sketch, "E41.8.1", {"start": v(-57.84, 53.08) * mm, "end": v(-58.84, 51.97) * mm});
            skLineSegment(sketch, "E41.8.2", {"start": v(-67.76, 60) * mm, "end": v(-58.84, 51.97) * mm});
            skLineSegment(sketch, "E41.8.3", {"start": v(-66.75, 61.11) * mm, "end": v(-57.84, 53.08) * mm});
            skLineSegment(sketch, "E41.9.0", {"start": v(-72.78, 53.8) * mm, "end": v(-73.66, 52.59) * mm});
            skLineSegment(sketch, "E41.9.1", {"start": v(-63.07, 46.75) * mm, "end": v(-63.95, 45.53) * mm});
            skLineSegment(sketch, "E41.9.2", {"start": v(-73.66, 52.59) * mm, "end": v(-63.95, 45.53) * mm});
            skLineSegment(sketch, "E41.9.3", {"start": v(-72.78, 53.8) * mm, "end": v(-63.07, 46.75) * mm});
            skLineSegment(sketch, "E41.10.0", {"start": v(-78, 45.9) * mm, "end": v(-78.75, 44.6) * mm});
            skLineSegment(sketch, "E41.10.1", {"start": v(-67.6, 39.9) * mm, "end": v(-68.36, 38.6) * mm});
            skLineSegment(sketch, "E41.10.2", {"start": v(-78.75, 44.6) * mm, "end": v(-68.36, 38.6) * mm});
            skLineSegment(sketch, "E41.10.3", {"start": v(-78, 45.9) * mm, "end": v(-67.6, 39.9) * mm});
            skLineSegment(sketch, "E41.11.0", {"start": v(-82.37, 37.5) * mm, "end": v(-82.98, 36.12) * mm});
            skLineSegment(sketch, "E41.11.1", {"start": v(-71.4, 32.61) * mm, "end": v(-72.02, 31.24) * mm});
            skLineSegment(sketch, "E41.11.2", {"start": v(-82.98, 36.12) * mm, "end": v(-72.02, 31.24) * mm});
            skLineSegment(sketch, "E41.11.3", {"start": v(-82.37, 37.5) * mm, "end": v(-71.4, 32.61) * mm});
            skLineSegment(sketch, "E41.12.0", {"start": v(-85.84, 28.68) * mm, "end": v(-86.3, 27.25) * mm});
            skLineSegment(sketch, "E41.12.1", {"start": v(-74.43, 24.97) * mm, "end": v(-74.89, 23.54) * mm});
            skLineSegment(sketch, "E41.12.2", {"start": v(-86.3, 27.25) * mm, "end": v(-74.89, 23.54) * mm});
            skLineSegment(sketch, "E41.12.3", {"start": v(-85.84, 28.68) * mm, "end": v(-74.43, 24.97) * mm});
            skLineSegment(sketch, "E41.13.0", {"start": v(-88.37, 19.55) * mm, "end": v(-88.68, 18.08) * mm});
            skLineSegment(sketch, "E41.13.1", {"start": v(-76.63, 17.05) * mm, "end": v(-76.94, 15.59) * mm});
            skLineSegment(sketch, "E41.13.2", {"start": v(-88.68, 18.08) * mm, "end": v(-76.94, 15.59) * mm});
            skLineSegment(sketch, "E41.13.3", {"start": v(-88.37, 19.55) * mm, "end": v(-76.63, 17.05) * mm});
            skLineSegment(sketch, "E41.14.0", {"start": v(-89.93, 10.2) * mm, "end": v(-90.08, 8.71) * mm});
            skLineSegment(sketch, "E41.14.1", {"start": v(-78, 8.95) * mm, "end": v(-78.15, 7.46) * mm});
            skLineSegment(sketch, "E41.14.2", {"start": v(-90.08, 8.71) * mm, "end": v(-78.15, 7.46) * mm});
            skLineSegment(sketch, "E41.14.3", {"start": v(-89.93, 10.2) * mm, "end": v(-78, 8.95) * mm});
            skLineSegment(sketch, "E41.15.0", {"start": v(-90.5, 0.75) * mm, "end": v(-90.5, -0.75) * mm});
            skLineSegment(sketch, "E41.15.1", {"start": v(-78.5, 0.75) * mm, "end": v(-78.5, -0.75) * mm});
            skLineSegment(sketch, "E41.15.2", {"start": v(-90.5, -0.75) * mm, "end": v(-78.5, -0.75) * mm});
            skLineSegment(sketch, "E41.15.3", {"start": v(-90.5, 0.75) * mm, "end": v(-78.5, 0.75) * mm});
            skLineSegment(sketch, "E41.16.0", {"start": v(-90.08, -8.71) * mm, "end": v(-89.93, -10.2) * mm});
            skLineSegment(sketch, "E41.16.1", {"start": v(-78.15, -7.46) * mm, "end": v(-78, -8.95) * mm});
            skLineSegment(sketch, "E41.16.2", {"start": v(-89.93, -10.2) * mm, "end": v(-78, -8.95) * mm});
            skLineSegment(sketch, "E41.16.3", {"start": v(-90.08, -8.71) * mm, "end": v(-78.15, -7.46) * mm});
            skLineSegment(sketch, "E41.17.0", {"start": v(-88.68, -18.08) * mm, "end": v(-88.37, -19.55) * mm});
            skLineSegment(sketch, "E41.17.1", {"start": v(-76.94, -15.59) * mm, "end": v(-76.63, -17.05) * mm});
            skLineSegment(sketch, "E41.17.2", {"start": v(-88.37, -19.55) * mm, "end": v(-76.63, -17.05) * mm});
            skLineSegment(sketch, "E41.17.3", {"start": v(-88.68, -18.08) * mm, "end": v(-76.94, -15.59) * mm});
            skLineSegment(sketch, "E41.18.0", {"start": v(-86.3, -27.25) * mm, "end": v(-85.84, -28.68) * mm});
            skLineSegment(sketch, "E41.18.1", {"start": v(-74.89, -23.54) * mm, "end": v(-74.43, -24.97) * mm});
            skLineSegment(sketch, "E41.18.2", {"start": v(-85.84, -28.68) * mm, "end": v(-74.43, -24.97) * mm});
            skLineSegment(sketch, "E41.18.3", {"start": v(-86.3, -27.25) * mm, "end": v(-74.89, -23.54) * mm});
            skLineSegment(sketch, "E41.19.0", {"start": v(-82.98, -36.12) * mm, "end": v(-82.37, -37.5) * mm});
            skLineSegment(sketch, "E41.19.1", {"start": v(-72.02, -31.24) * mm, "end": v(-71.4, -32.61) * mm});
            skLineSegment(sketch, "E41.19.2", {"start": v(-82.37, -37.5) * mm, "end": v(-71.4, -32.61) * mm});
            skLineSegment(sketch, "E41.19.3", {"start": v(-82.98, -36.12) * mm, "end": v(-72.02, -31.24) * mm});
            skLineSegment(sketch, "E41.20.0", {"start": v(-78.75, -44.6) * mm, "end": v(-78, -45.9) * mm});
            skLineSegment(sketch, "E41.20.1", {"start": v(-68.36, -38.6) * mm, "end": v(-67.6, -39.9) * mm});
            skLineSegment(sketch, "E41.20.2", {"start": v(-78, -45.9) * mm, "end": v(-67.6, -39.9) * mm});
            skLineSegment(sketch, "E41.20.3", {"start": v(-78.75, -44.6) * mm, "end": v(-68.36, -38.6) * mm});
            skLineSegment(sketch, "E41.21.0", {"start": v(-73.66, -52.59) * mm, "end": v(-72.78, -53.8) * mm});
            skLineSegment(sketch, "E41.21.1", {"start": v(-63.95, -45.53) * mm, "end": v(-63.07, -46.75) * mm});
            skLineSegment(sketch, "E41.21.2", {"start": v(-72.78, -53.8) * mm, "end": v(-63.07, -46.75) * mm});
            skLineSegment(sketch, "E41.21.3", {"start": v(-73.66, -52.59) * mm, "end": v(-63.95, -45.53) * mm});
            skLineSegment(sketch, "E41.22.0", {"start": v(-67.76, -60) * mm, "end": v(-66.75, -61.11) * mm});
            skLineSegment(sketch, "E41.22.1", {"start": v(-58.84, -51.97) * mm, "end": v(-57.84, -53.08) * mm});
            skLineSegment(sketch, "E41.22.2", {"start": v(-66.75, -61.11) * mm, "end": v(-57.84, -53.08) * mm});
            skLineSegment(sketch, "E41.22.3", {"start": v(-67.76, -60) * mm, "end": v(-58.84, -51.97) * mm});
            skLineSegment(sketch, "E41.23.0", {"start": v(-61.11, -66.75) * mm, "end": v(-60, -67.76) * mm});
            skLineSegment(sketch, "E41.23.1", {"start": v(-53.08, -57.84) * mm, "end": v(-51.97, -58.84) * mm});
            skLineSegment(sketch, "E41.23.2", {"start": v(-60, -67.76) * mm, "end": v(-51.97, -58.84) * mm});
            skLineSegment(sketch, "E41.23.3", {"start": v(-61.11, -66.75) * mm, "end": v(-53.08, -57.84) * mm});
            skLineSegment(sketch, "E41.24.0", {"start": v(-53.8, -72.78) * mm, "end": v(-52.59, -73.66) * mm});
            skLineSegment(sketch, "E41.24.1", {"start": v(-46.75, -63.07) * mm, "end": v(-45.53, -63.95) * mm});
            skLineSegment(sketch, "E41.24.2", {"start": v(-52.59, -73.66) * mm, "end": v(-45.53, -63.95) * mm});
            skLineSegment(sketch, "E41.24.3", {"start": v(-53.8, -72.78) * mm, "end": v(-46.75, -63.07) * mm});
            skLineSegment(sketch, "E41.25.0", {"start": v(-45.9, -78) * mm, "end": v(-44.6, -78.75) * mm});
            skLineSegment(sketch, "E41.25.1", {"start": v(-39.9, -67.6) * mm, "end": v(-38.6, -68.36) * mm});
            skLineSegment(sketch, "E41.25.2", {"start": v(-44.6, -78.75) * mm, "end": v(-38.6, -68.36) * mm});
            skLineSegment(sketch, "E41.25.3", {"start": v(-45.9, -78) * mm, "end": v(-39.9, -67.6) * mm});
            skLineSegment(sketch, "E41.26.0", {"start": v(-37.5, -82.37) * mm, "end": v(-36.12, -82.98) * mm});
            skLineSegment(sketch, "E41.26.1", {"start": v(-32.61, -71.4) * mm, "end": v(-31.24, -72.02) * mm});
            skLineSegment(sketch, "E41.26.2", {"start": v(-36.12, -82.98) * mm, "end": v(-31.24, -72.02) * mm});
            skLineSegment(sketch, "E41.26.3", {"start": v(-37.5, -82.37) * mm, "end": v(-32.61, -71.4) * mm});
            skLineSegment(sketch, "E41.27.0", {"start": v(-28.68, -85.84) * mm, "end": v(-27.25, -86.3) * mm});
            skLineSegment(sketch, "E41.27.1", {"start": v(-24.97, -74.43) * mm, "end": v(-23.54, -74.89) * mm});
            skLineSegment(sketch, "E41.27.2", {"start": v(-27.25, -86.3) * mm, "end": v(-23.54, -74.89) * mm});
            skLineSegment(sketch, "E41.27.3", {"start": v(-28.68, -85.84) * mm, "end": v(-24.97, -74.43) * mm});
            skLineSegment(sketch, "E41.28.0", {"start": v(-19.55, -88.37) * mm, "end": v(-18.08, -88.68) * mm});
            skLineSegment(sketch, "E41.28.1", {"start": v(-17.05, -76.63) * mm, "end": v(-15.59, -76.94) * mm});
            skLineSegment(sketch, "E41.28.2", {"start": v(-18.08, -88.68) * mm, "end": v(-15.59, -76.94) * mm});
            skLineSegment(sketch, "E41.28.3", {"start": v(-19.55, -88.37) * mm, "end": v(-17.05, -76.63) * mm});
            skLineSegment(sketch, "E41.29.0", {"start": v(-10.2, -89.93) * mm, "end": v(-8.71, -90.08) * mm});
            skLineSegment(sketch, "E41.29.1", {"start": v(-8.95, -78) * mm, "end": v(-7.46, -78.15) * mm});
            skLineSegment(sketch, "E41.29.2", {"start": v(-8.71, -90.08) * mm, "end": v(-7.46, -78.15) * mm});
            skLineSegment(sketch, "E41.29.3", {"start": v(-10.2, -89.93) * mm, "end": v(-8.95, -78) * mm});
            skLineSegment(sketch, "E41.30.0", {"start": v(-0.75, -90.5) * mm, "end": v(0.75, -90.5) * mm});
            skLineSegment(sketch, "E41.30.1", {"start": v(-0.75, -78.5) * mm, "end": v(0.75, -78.5) * mm});
            skLineSegment(sketch, "E41.30.2", {"start": v(0.75, -90.5) * mm, "end": v(0.75, -78.5) * mm});
            skLineSegment(sketch, "E41.30.3", {"start": v(-0.75, -90.5) * mm, "end": v(-0.75, -78.5) * mm});
            skLineSegment(sketch, "E41.31.0", {"start": v(8.71, -90.08) * mm, "end": v(10.2, -89.93) * mm});
            skLineSegment(sketch, "E41.31.1", {"start": v(7.46, -78.15) * mm, "end": v(8.95, -78) * mm});
            skLineSegment(sketch, "E41.31.2", {"start": v(10.2, -89.93) * mm, "end": v(8.95, -78) * mm});
            skLineSegment(sketch, "E41.31.3", {"start": v(8.71, -90.08) * mm, "end": v(7.46, -78.15) * mm});
            skLineSegment(sketch, "E41.32.0", {"start": v(18.08, -88.68) * mm, "end": v(19.55, -88.37) * mm});
            skLineSegment(sketch, "E41.32.1", {"start": v(15.59, -76.94) * mm, "end": v(17.05, -76.63) * mm});
            skLineSegment(sketch, "E41.32.2", {"start": v(19.55, -88.37) * mm, "end": v(17.05, -76.63) * mm});
            skLineSegment(sketch, "E41.32.3", {"start": v(18.08, -88.68) * mm, "end": v(15.59, -76.94) * mm});
            skLineSegment(sketch, "E41.33.0", {"start": v(27.25, -86.3) * mm, "end": v(28.68, -85.84) * mm});
            skLineSegment(sketch, "E41.33.1", {"start": v(23.54, -74.89) * mm, "end": v(24.97, -74.43) * mm});
            skLineSegment(sketch, "E41.33.2", {"start": v(28.68, -85.84) * mm, "end": v(24.97, -74.43) * mm});
            skLineSegment(sketch, "E41.33.3", {"start": v(27.25, -86.3) * mm, "end": v(23.54, -74.89) * mm});
            skLineSegment(sketch, "E41.34.0", {"start": v(36.12, -82.98) * mm, "end": v(37.5, -82.37) * mm});
            skLineSegment(sketch, "E41.34.1", {"start": v(31.24, -72.02) * mm, "end": v(32.61, -71.4) * mm});
            skLineSegment(sketch, "E41.34.2", {"start": v(37.5, -82.37) * mm, "end": v(32.61, -71.4) * mm});
            skLineSegment(sketch, "E41.34.3", {"start": v(36.12, -82.98) * mm, "end": v(31.24, -72.02) * mm});
            skLineSegment(sketch, "E41.35.0", {"start": v(44.6, -78.75) * mm, "end": v(45.9, -78) * mm});
            skLineSegment(sketch, "E41.35.1", {"start": v(38.6, -68.36) * mm, "end": v(39.9, -67.6) * mm});
            skLineSegment(sketch, "E41.35.2", {"start": v(45.9, -78) * mm, "end": v(39.9, -67.6) * mm});
            skLineSegment(sketch, "E41.35.3", {"start": v(44.6, -78.75) * mm, "end": v(38.6, -68.36) * mm});
            skLineSegment(sketch, "E41.36.0", {"start": v(52.59, -73.66) * mm, "end": v(53.8, -72.78) * mm});
            skLineSegment(sketch, "E41.36.1", {"start": v(45.53, -63.95) * mm, "end": v(46.75, -63.07) * mm});
            skLineSegment(sketch, "E41.36.2", {"start": v(53.8, -72.78) * mm, "end": v(46.75, -63.07) * mm});
            skLineSegment(sketch, "E41.36.3", {"start": v(52.59, -73.66) * mm, "end": v(45.53, -63.95) * mm});
            skLineSegment(sketch, "E41.37.0", {"start": v(60, -67.76) * mm, "end": v(61.11, -66.75) * mm});
            skLineSegment(sketch, "E41.37.1", {"start": v(51.97, -58.84) * mm, "end": v(53.08, -57.84) * mm});
            skLineSegment(sketch, "E41.37.2", {"start": v(61.11, -66.75) * mm, "end": v(53.08, -57.84) * mm});
            skLineSegment(sketch, "E41.37.3", {"start": v(60, -67.76) * mm, "end": v(51.97, -58.84) * mm});
            skLineSegment(sketch, "E41.38.0", {"start": v(66.75, -61.11) * mm, "end": v(67.76, -60) * mm});
            skLineSegment(sketch, "E41.38.1", {"start": v(57.84, -53.08) * mm, "end": v(58.84, -51.97) * mm});
            skLineSegment(sketch, "E41.38.2", {"start": v(67.76, -60) * mm, "end": v(58.84, -51.97) * mm});
            skLineSegment(sketch, "E41.38.3", {"start": v(66.75, -61.11) * mm, "end": v(57.84, -53.08) * mm});
            skLineSegment(sketch, "E41.39.0", {"start": v(72.78, -53.8) * mm, "end": v(73.66, -52.59) * mm});
            skLineSegment(sketch, "E41.39.1", {"start": v(63.07, -46.75) * mm, "end": v(63.95, -45.53) * mm});
            skLineSegment(sketch, "E41.39.2", {"start": v(73.66, -52.59) * mm, "end": v(63.95, -45.53) * mm});
            skLineSegment(sketch, "E41.39.3", {"start": v(72.78, -53.8) * mm, "end": v(63.07, -46.75) * mm});
            skLineSegment(sketch, "E41.40.0", {"start": v(78, -45.9) * mm, "end": v(78.75, -44.6) * mm});
            skLineSegment(sketch, "E41.40.1", {"start": v(67.6, -39.9) * mm, "end": v(68.36, -38.6) * mm});
            skLineSegment(sketch, "E41.40.2", {"start": v(78.75, -44.6) * mm, "end": v(68.36, -38.6) * mm});
            skLineSegment(sketch, "E41.40.3", {"start": v(78, -45.9) * mm, "end": v(67.6, -39.9) * mm});
            skLineSegment(sketch, "E41.41.0", {"start": v(82.37, -37.5) * mm, "end": v(82.98, -36.12) * mm});
            skLineSegment(sketch, "E41.41.1", {"start": v(71.4, -32.61) * mm, "end": v(72.02, -31.24) * mm});
            skLineSegment(sketch, "E41.41.2", {"start": v(82.98, -36.12) * mm, "end": v(72.02, -31.24) * mm});
            skLineSegment(sketch, "E41.41.3", {"start": v(82.37, -37.5) * mm, "end": v(71.4, -32.61) * mm});
            skLineSegment(sketch, "E41.42.0", {"start": v(85.84, -28.68) * mm, "end": v(86.3, -27.25) * mm});
            skLineSegment(sketch, "E41.42.1", {"start": v(74.43, -24.97) * mm, "end": v(74.89, -23.54) * mm});
            skLineSegment(sketch, "E41.42.2", {"start": v(86.3, -27.25) * mm, "end": v(74.89, -23.54) * mm});
            skLineSegment(sketch, "E41.42.3", {"start": v(85.84, -28.68) * mm, "end": v(74.43, -24.97) * mm});
            skLineSegment(sketch, "E41.43.0", {"start": v(88.37, -19.55) * mm, "end": v(88.68, -18.08) * mm});
            skLineSegment(sketch, "E41.43.1", {"start": v(76.63, -17.05) * mm, "end": v(76.94, -15.59) * mm});
            skLineSegment(sketch, "E41.43.2", {"start": v(88.68, -18.08) * mm, "end": v(76.94, -15.59) * mm});
            skLineSegment(sketch, "E41.43.3", {"start": v(88.37, -19.55) * mm, "end": v(76.63, -17.05) * mm});
            skLineSegment(sketch, "E41.44.0", {"start": v(89.93, -10.2) * mm, "end": v(90.08, -8.71) * mm});
            skLineSegment(sketch, "E41.44.1", {"start": v(78, -8.95) * mm, "end": v(78.15, -7.46) * mm});
            skLineSegment(sketch, "E41.44.2", {"start": v(90.08, -8.71) * mm, "end": v(78.15, -7.46) * mm});
            skLineSegment(sketch, "E41.44.3", {"start": v(89.93, -10.2) * mm, "end": v(78, -8.95) * mm});
            skLineSegment(sketch, "E41.45.0", {"start": v(90.5, -0.75) * mm, "end": v(90.5, 0.75) * mm});
            skLineSegment(sketch, "E41.45.1", {"start": v(78.5, -0.75) * mm, "end": v(78.5, 0.75) * mm});
            skLineSegment(sketch, "E41.45.2", {"start": v(90.5, 0.75) * mm, "end": v(78.5, 0.75) * mm});
            skLineSegment(sketch, "E41.45.3", {"start": v(90.5, -0.75) * mm, "end": v(78.5, -0.75) * mm});
            skLineSegment(sketch, "E41.46.0", {"start": v(90.08, 8.71) * mm, "end": v(89.93, 10.2) * mm});
            skLineSegment(sketch, "E41.46.1", {"start": v(78.15, 7.46) * mm, "end": v(78, 8.95) * mm});
            skLineSegment(sketch, "E41.46.2", {"start": v(89.93, 10.2) * mm, "end": v(78, 8.95) * mm});
            skLineSegment(sketch, "E41.46.3", {"start": v(90.08, 8.71) * mm, "end": v(78.15, 7.46) * mm});
            skLineSegment(sketch, "E41.47.0", {"start": v(88.68, 18.08) * mm, "end": v(88.37, 19.55) * mm});
            skLineSegment(sketch, "E41.47.1", {"start": v(76.94, 15.59) * mm, "end": v(76.63, 17.05) * mm});
            skLineSegment(sketch, "E41.47.2", {"start": v(88.37, 19.55) * mm, "end": v(76.63, 17.05) * mm});
            skLineSegment(sketch, "E41.47.3", {"start": v(88.68, 18.08) * mm, "end": v(76.94, 15.59) * mm});
            skLineSegment(sketch, "E41.48.0", {"start": v(86.3, 27.25) * mm, "end": v(85.84, 28.68) * mm});
            skLineSegment(sketch, "E41.48.1", {"start": v(74.89, 23.54) * mm, "end": v(74.43, 24.97) * mm});
            skLineSegment(sketch, "E41.48.2", {"start": v(85.84, 28.68) * mm, "end": v(74.43, 24.97) * mm});
            skLineSegment(sketch, "E41.48.3", {"start": v(86.3, 27.25) * mm, "end": v(74.89, 23.54) * mm});
            skLineSegment(sketch, "E41.49.0", {"start": v(82.98, 36.12) * mm, "end": v(82.37, 37.5) * mm});
            skLineSegment(sketch, "E41.49.1", {"start": v(72.02, 31.24) * mm, "end": v(71.4, 32.61) * mm});
            skLineSegment(sketch, "E41.49.2", {"start": v(82.37, 37.5) * mm, "end": v(71.4, 32.61) * mm});
            skLineSegment(sketch, "E41.49.3", {"start": v(82.98, 36.12) * mm, "end": v(72.02, 31.24) * mm});
            skLineSegment(sketch, "E41.50.0", {"start": v(78.75, 44.6) * mm, "end": v(78, 45.9) * mm});
            skLineSegment(sketch, "E41.50.1", {"start": v(68.36, 38.6) * mm, "end": v(67.6, 39.9) * mm});
            skLineSegment(sketch, "E41.50.2", {"start": v(78, 45.9) * mm, "end": v(67.6, 39.9) * mm});
            skLineSegment(sketch, "E41.50.3", {"start": v(78.75, 44.6) * mm, "end": v(68.36, 38.6) * mm});
            skLineSegment(sketch, "E41.51.0", {"start": v(73.66, 52.59) * mm, "end": v(72.78, 53.8) * mm});
            skLineSegment(sketch, "E41.51.1", {"start": v(63.95, 45.53) * mm, "end": v(63.07, 46.75) * mm});
            skLineSegment(sketch, "E41.51.2", {"start": v(72.78, 53.8) * mm, "end": v(63.07, 46.75) * mm});
            skLineSegment(sketch, "E41.51.3", {"start": v(73.66, 52.59) * mm, "end": v(63.95, 45.53) * mm});
            skLineSegment(sketch, "E41.52.0", {"start": v(67.76, 60) * mm, "end": v(66.75, 61.11) * mm});
            skLineSegment(sketch, "E41.52.1", {"start": v(58.84, 51.97) * mm, "end": v(57.84, 53.08) * mm});
            skLineSegment(sketch, "E41.52.2", {"start": v(66.75, 61.11) * mm, "end": v(57.84, 53.08) * mm});
            skLineSegment(sketch, "E41.52.3", {"start": v(67.76, 60) * mm, "end": v(58.84, 51.97) * mm});
            skLineSegment(sketch, "E41.53.0", {"start": v(61.11, 66.75) * mm, "end": v(60, 67.76) * mm});
            skLineSegment(sketch, "E41.53.1", {"start": v(53.08, 57.84) * mm, "end": v(51.97, 58.84) * mm});
            skLineSegment(sketch, "E41.53.2", {"start": v(60, 67.76) * mm, "end": v(51.97, 58.84) * mm});
            skLineSegment(sketch, "E41.53.3", {"start": v(61.11, 66.75) * mm, "end": v(53.08, 57.84) * mm});
            skLineSegment(sketch, "E41.54.0", {"start": v(53.8, 72.78) * mm, "end": v(52.59, 73.66) * mm});
            skLineSegment(sketch, "E41.54.1", {"start": v(46.75, 63.07) * mm, "end": v(45.53, 63.95) * mm});
            skLineSegment(sketch, "E41.54.2", {"start": v(52.59, 73.66) * mm, "end": v(45.53, 63.95) * mm});
            skLineSegment(sketch, "E41.54.3", {"start": v(53.8, 72.78) * mm, "end": v(46.75, 63.07) * mm});
            skLineSegment(sketch, "E41.55.0", {"start": v(45.9, 78) * mm, "end": v(44.6, 78.75) * mm});
            skLineSegment(sketch, "E41.55.1", {"start": v(39.9, 67.6) * mm, "end": v(38.6, 68.36) * mm});
            skLineSegment(sketch, "E41.55.2", {"start": v(44.6, 78.75) * mm, "end": v(38.6, 68.36) * mm});
            skLineSegment(sketch, "E41.55.3", {"start": v(45.9, 78) * mm, "end": v(39.9, 67.6) * mm});
            skLineSegment(sketch, "E41.56.0", {"start": v(37.5, 82.37) * mm, "end": v(36.12, 82.98) * mm});
            skLineSegment(sketch, "E41.56.1", {"start": v(32.61, 71.4) * mm, "end": v(31.24, 72.02) * mm});
            skLineSegment(sketch, "E41.56.2", {"start": v(36.12, 82.98) * mm, "end": v(31.24, 72.02) * mm});
            skLineSegment(sketch, "E41.56.3", {"start": v(37.5, 82.37) * mm, "end": v(32.61, 71.4) * mm});
            skLineSegment(sketch, "E41.57.0", {"start": v(28.68, 85.84) * mm, "end": v(27.25, 86.3) * mm});
            skLineSegment(sketch, "E41.57.1", {"start": v(24.97, 74.43) * mm, "end": v(23.54, 74.89) * mm});
            skLineSegment(sketch, "E41.57.2", {"start": v(27.25, 86.3) * mm, "end": v(23.54, 74.89) * mm});
            skLineSegment(sketch, "E41.57.3", {"start": v(28.68, 85.84) * mm, "end": v(24.97, 74.43) * mm});
            skLineSegment(sketch, "E41.58.0", {"start": v(19.55, 88.37) * mm, "end": v(18.08, 88.68) * mm});
            skLineSegment(sketch, "E41.58.1", {"start": v(17.05, 76.63) * mm, "end": v(15.59, 76.94) * mm});
            skLineSegment(sketch, "E41.58.2", {"start": v(18.08, 88.68) * mm, "end": v(15.59, 76.94) * mm});
            skLineSegment(sketch, "E41.58.3", {"start": v(19.55, 88.37) * mm, "end": v(17.05, 76.63) * mm});
            skLineSegment(sketch, "E41.59.0", {"start": v(10.2, 89.93) * mm, "end": v(8.71, 90.08) * mm});
            skLineSegment(sketch, "E41.59.1", {"start": v(8.95, 78) * mm, "end": v(7.46, 78.15) * mm});
            skLineSegment(sketch, "E41.59.2", {"start": v(8.71, 90.08) * mm, "end": v(7.46, 78.15) * mm});
            skLineSegment(sketch, "E41.59.3", {"start": v(10.2, 89.93) * mm, "end": v(8.95, 78) * mm});
            skPoint(sketch, "E41.center", {"position": v(0, 0) * mm});
            skSolve(sketch);
        }
        {
            var Q0;
            Q0 = qSketchRegion(id + "F27", true);
            extrude(context, id + "F28", {"entities" : qUnion([Q0]), "operationType" : NewBodyOperationType.REMOVE, "oppositeDirection" : true, "depth" : 0.2 * mm, "offsetDistance" : 25 * mm});
        }
        {
            var Q0;
            Q0=makeQuery(id+"F26.boolean.opBoolean","COPY",FACE,{"derivedFrom":makeQuery(id+"F26.opExtrude","CAP_FACE",FACE,{"disambiguationData":[OSD([sQuery(id+"F25.wireOp",EDGE,"E38.bottom"),sQuery(id+"F25.wireOp",EDGE,"E38.top"),sQuery(id+"F25.wireOp",EDGE,"E38.left"),sQuery(id+"F25.wireOp",EDGE,"E38.right")])],"isStart":false})});
            extrude(context, id + "F29", {"entities" : qUnion([Q0]), "depth" : 1 * mm, "offsetDistance" : 25 * mm});
        }
        {
            var Q0;
            Q0=makeQuery(id+"F28.boolean.opBoolean","COPY",FACE,{"derivedFrom":makeQuery(id+"F28.opExtrude","CAP_FACE",FACE,{"disambiguationData":[OSD([sQuery(id+"F27.wireOp",EDGE,"E41.59.0"),sQuery(id+"F27.wireOp",EDGE,"E41.59.1"),sQuery(id+"F27.wireOp",EDGE,"E41.59.2"),sQuery(id+"F27.wireOp",EDGE,"E41.59.3")])],"isStart":false})});
            extrude(context, id + "F30", {"entities" : qUnion([Q0]), "depth" : 0.4 * mm, "offsetDistance" : 25 * mm});
        }
        {
            var Q0;
            Q0=makeQuery(id+"F15.opExtrude","CAP_FACE",FACE,{"disambiguationData":[OSD([sQuery(id+"F14.wireOp",EDGE,"E19.0.0"),sQuery(id+"F14.wireOp",EDGE,"E20"),sQuery(id+"F14.wireOp",EDGE,"E21"),sQuery(id+"F14.wireOp",EDGE,"E22"),sQuery(id+"F14.wireOp",EDGE,"E23.MirrorCS"),sQuery(id+"F14.wireOp",EDGE,"E24.MirrorCS"),sQuery(id+"F14.wireOp",EDGE,"E25.1.0"),sQuery(id+"F14.wireOp",EDGE,"E25.1.1"),sQuery(id+"F14.wireOp",EDGE,"E25.1.2"),sQuery(id+"F14.wireOp",EDGE,"E25.1.3"),sQuery(id+"F14.wireOp",EDGE,"E25.2.0"),sQuery(id+"F14.wireOp",EDGE,"E25.2.1"),sQuery(id+"F14.wireOp",EDGE,"E25.2.2"),sQuery(id+"F14.wireOp",EDGE,"E25.2.3"),sQuery(id+"F14.wireOp",EDGE,"E25.3.0"),sQuery(id+"F14.wireOp",EDGE,"E25.3.1"),sQuery(id+"F14.wireOp",EDGE,"E25.3.2"),sQuery(id+"F14.wireOp",EDGE,"E25.3.3"),sQuery(id+"F14.wireOp",EDGE,"E25.4.0"),sQuery(id+"F14.wireOp",EDGE,"E25.4.1"),sQuery(id+"F14.wireOp",EDGE,"E25.4.2"),sQuery(id+"F14.wireOp",EDGE,"E25.4.3"),sQuery(id+"F14.wireOp",EDGE,"E25.5.0"),sQuery(id+"F14.wireOp",EDGE,"E25.5.1"),sQuery(id+"F14.wireOp",EDGE,"E25.5.2"),sQuery(id+"F14.wireOp",EDGE,"E25.5.3"),sQuery(id+"F14.wireOp",EDGE,"E25.6.0"),sQuery(id+"F14.wireOp",EDGE,"E25.6.1"),sQuery(id+"F14.wireOp",EDGE,"E25.6.2"),sQuery(id+"F14.wireOp",EDGE,"E25.6.3"),sQuery(id+"F14.wireOp",EDGE,"E25.7.0"),sQuery(id+"F14.wireOp",EDGE,"E25.7.1"),sQuery(id+"F14.wireOp",EDGE,"E25.7.2"),sQuery(id+"F14.wireOp",EDGE,"E25.7.3"),sQuery(id+"F14.wireOp",EDGE,"E25.8.0"),sQuery(id+"F14.wireOp",EDGE,"E25.8.1"),sQuery(id+"F14.wireOp",EDGE,"E25.8.2"),sQuery(id+"F14.wireOp",EDGE,"E25.8.3"),sQuery(id+"F14.wireOp",EDGE,"E25.9.0"),sQuery(id+"F14.wireOp",EDGE,"E25.9.1"),sQuery(id+"F14.wireOp",EDGE,"E25.9.2"),sQuery(id+"F14.wireOp",EDGE,"E25.9.3"),sQuery(id+"F14.wireOp",EDGE,"E25.10.0"),sQuery(id+"F14.wireOp",EDGE,"E25.10.1"),sQuery(id+"F14.wireOp",EDGE,"E25.10.2"),sQuery(id+"F14.wireOp",EDGE,"E25.10.3"),sQuery(id+"F14.wireOp",EDGE,"E25.11.0"),sQuery(id+"F14.wireOp",EDGE,"E25.11.1"),sQuery(id+"F14.wireOp",EDGE,"E25.11.2"),sQuery(id+"F14.wireOp",EDGE,"E25.11.3"),sQuery(id+"F14.wireOp",EDGE,"E25.12.0"),sQuery(id+"F14.wireOp",EDGE,"E25.12.1"),sQuery(id+"F14.wireOp",EDGE,"E25.12.2"),sQuery(id+"F14.wireOp",EDGE,"E25.12.3"),sQuery(id+"F14.wireOp",EDGE,"E25.13.0"),sQuery(id+"F14.wireOp",EDGE,"E25.13.1"),sQuery(id+"F14.wireOp",EDGE,"E25.13.2"),sQuery(id+"F14.wireOp",EDGE,"E25.13.3"),sQuery(id+"F14.wireOp",EDGE,"E25.14.0"),sQuery(id+"F14.wireOp",EDGE,"E25.14.1"),sQuery(id+"F14.wireOp",EDGE,"E25.14.2"),sQuery(id+"F14.wireOp",EDGE,"E25.14.3"),sQuery(id+"F14.wireOp",EDGE,"E25.15.0"),sQuery(id+"F14.wireOp",EDGE,"E25.15.1"),sQuery(id+"F14.wireOp",EDGE,"E25.15.2"),sQuery(id+"F14.wireOp",EDGE,"E25.15.3"),sQuery(id+"F14.wireOp",EDGE,"E25.16.0"),sQuery(id+"F14.wireOp",EDGE,"E25.16.1"),sQuery(id+"F14.wireOp",EDGE,"E25.16.2"),sQuery(id+"F14.wireOp",EDGE,"E25.16.3"),sQuery(id+"F14.wireOp",EDGE,"E25.17.0"),sQuery(id+"F14.wireOp",EDGE,"E25.17.1"),sQuery(id+"F14.wireOp",EDGE,"E25.17.2"),sQuery(id+"F14.wireOp",EDGE,"E25.17.3"),sQuery(id+"F14.wireOp",EDGE,"E25.18.0"),sQuery(id+"F14.wireOp",EDGE,"E25.18.1"),sQuery(id+"F14.wireOp",EDGE,"E25.18.2"),sQuery(id+"F14.wireOp",EDGE,"E25.18.3"),sQuery(id+"F14.wireOp",EDGE,"E25.19.0"),sQuery(id+"F14.wireOp",EDGE,"E25.19.1"),sQuery(id+"F14.wireOp",EDGE,"E25.19.2"),sQuery(id+"F14.wireOp",EDGE,"E25.19.3"),sQuery(id+"F14.wireOp",EDGE,"E25.20.0"),sQuery(id+"F14.wireOp",EDGE,"E25.20.1"),sQuery(id+"F14.wireOp",EDGE,"E25.20.2"),sQuery(id+"F14.wireOp",EDGE,"E25.20.3"),sQuery(id+"F14.wireOp",EDGE,"E25.21.0"),sQuery(id+"F14.wireOp",EDGE,"E25.21.1"),sQuery(id+"F14.wireOp",EDGE,"E25.21.2"),sQuery(id+"F14.wireOp",EDGE,"E25.21.3"),sQuery(id+"F14.wireOp",EDGE,"E25.22.0"),sQuery(id+"F14.wireOp",EDGE,"E25.22.1"),sQuery(id+"F14.wireOp",EDGE,"E25.22.2"),sQuery(id+"F14.wireOp",EDGE,"E25.22.3"),sQuery(id+"F14.wireOp",EDGE,"E25.23.0"),sQuery(id+"F14.wireOp",EDGE,"E25.23.1"),sQuery(id+"F14.wireOp",EDGE,"E25.23.2"),sQuery(id+"F14.wireOp",EDGE,"E25.23.3"),sQuery(id+"F14.wireOp",EDGE,"E25.24.0"),sQuery(id+"F14.wireOp",EDGE,"E25.24.1"),sQuery(id+"F14.wireOp",EDGE,"E25.24.2"),sQuery(id+"F14.wireOp",EDGE,"E25.24.3"),sQuery(id+"F14.wireOp",EDGE,"E25.25.0"),sQuery(id+"F14.wireOp",EDGE,"E25.25.1"),sQuery(id+"F14.wireOp",EDGE,"E25.25.2"),sQuery(id+"F14.wireOp",EDGE,"E25.25.3"),sQuery(id+"F14.wireOp",EDGE,"E25.26.0"),sQuery(id+"F14.wireOp",EDGE,"E25.26.1"),sQuery(id+"F14.wireOp",EDGE,"E25.26.2"),sQuery(id+"F14.wireOp",EDGE,"E25.26.3"),sQuery(id+"F14.wireOp",EDGE,"E25.27.0"),sQuery(id+"F14.wireOp",EDGE,"E25.27.1"),sQuery(id+"F14.wireOp",EDGE,"E25.27.2"),sQuery(id+"F14.wireOp",EDGE,"E25.27.3"),sQuery(id+"F14.wireOp",EDGE,"E25.28.0"),sQuery(id+"F14.wireOp",EDGE,"E25.28.1"),sQuery(id+"F14.wireOp",EDGE,"E25.28.2"),sQuery(id+"F14.wireOp",EDGE,"E25.28.3"),sQuery(id+"F14.wireOp",EDGE,"E25.29.0"),sQuery(id+"F14.wireOp",EDGE,"E25.29.1"),sQuery(id+"F14.wireOp",EDGE,"E25.29.2"),sQuery(id+"F14.wireOp",EDGE,"E25.29.3"),sQuery(id+"F14.wireOp",EDGE,"E25.30.0"),sQuery(id+"F14.wireOp",EDGE,"E25.30.1"),sQuery(id+"F14.wireOp",EDGE,"E25.30.2"),sQuery(id+"F14.wireOp",EDGE,"E25.30.3"),sQuery(id+"F14.wireOp",EDGE,"E25.31.0"),sQuery(id+"F14.wireOp",EDGE,"E25.31.1"),sQuery(id+"F14.wireOp",EDGE,"E25.31.2"),sQuery(id+"F14.wireOp",EDGE,"E25.31.3"),sQuery(id+"F14.wireOp",EDGE,"E25.32.0"),sQuery(id+"F14.wireOp",EDGE,"E25.32.1"),sQuery(id+"F14.wireOp",EDGE,"E25.32.2"),sQuery(id+"F14.wireOp",EDGE,"E25.32.3"),sQuery(id+"F14.wireOp",EDGE,"E25.33.0"),sQuery(id+"F14.wireOp",EDGE,"E25.33.1"),sQuery(id+"F14.wireOp",EDGE,"E25.33.2"),sQuery(id+"F14.wireOp",EDGE,"E25.33.3"),sQuery(id+"F14.wireOp",EDGE,"E25.34.0"),sQuery(id+"F14.wireOp",EDGE,"E25.34.1"),sQuery(id+"F14.wireOp",EDGE,"E25.34.2"),sQuery(id+"F14.wireOp",EDGE,"E25.34.3"),sQuery(id+"F14.wireOp",EDGE,"E25.35.0"),sQuery(id+"F14.wireOp",EDGE,"E25.35.1"),sQuery(id+"F14.wireOp",EDGE,"E25.35.2"),sQuery(id+"F14.wireOp",EDGE,"E25.35.3"),sQuery(id+"F14.wireOp",EDGE,"E25.36.0"),sQuery(id+"F14.wireOp",EDGE,"E25.36.1"),sQuery(id+"F14.wireOp",EDGE,"E25.36.2"),sQuery(id+"F14.wireOp",EDGE,"E25.36.3"),sQuery(id+"F14.wireOp",EDGE,"E25.37.0"),sQuery(id+"F14.wireOp",EDGE,"E25.37.1"),sQuery(id+"F14.wireOp",EDGE,"E25.37.2"),sQuery(id+"F14.wireOp",EDGE,"E25.37.3"),sQuery(id+"F14.wireOp",EDGE,"E25.38.0"),sQuery(id+"F14.wireOp",EDGE,"E25.38.1"),sQuery(id+"F14.wireOp",EDGE,"E25.38.2"),sQuery(id+"F14.wireOp",EDGE,"E25.38.3"),sQuery(id+"F14.wireOp",EDGE,"E25.39.0"),sQuery(id+"F14.wireOp",EDGE,"E25.39.1"),sQuery(id+"F14.wireOp",EDGE,"E25.39.2"),sQuery(id+"F14.wireOp",EDGE,"E25.39.3")])],"isStart":false});
            var sketch = newSketch(context, id + "F31", { "sketchPlane" : qUnion([Q0])});
            skCircle(sketch, "E42.0", {"center": v(0, 0) * mm, "radius": 3 * mm});
            skCircle(sketch, "E43.0.0", {"center": v(0, 0) * mm, "radius": 98 * mm});
            skCircle(sketch, "E44.0", {"center": v(0, 0) * mm, "radius": 5 * mm});
            skSolve(sketch);
        }
        {
            var Q0;
            Q0=makeQuery(id+"F31.imprint","IMPRINT",FACE,{"disambiguationData":[TD([[makeQuery(id+"F31.imprint","IMPRINT",EDGE,{"derivedFrom":sQuery(id+"F31.wireOp",EDGE,"E42.0")}),-1.0]])]});
            extrude(context, id + "F32", {"entities" : qUnion([Q0]), "operationType" : NewBodyOperationType.ADD, "depth" : 5 * mm, "offsetDistance" : 25 * mm});
        }
        {
            var Q0;
            Q0=makeQuery(id+"F32.opExtrude","CAP_FACE",FACE,{"disambiguationData":[OSD([sQuery(id+"F31.wireOp",EDGE,"E42.0"),sQuery(id+"F31.wireOp",EDGE,"E44.0")])],"isStart":false});
            var sketch = newSketch(context, id + "F33", { "sketchPlane" : qUnion([Q0])});
            skCircle(sketch, "E45.0", {"center": v(0, 0) * mm, "radius": 3 * mm});
            skCircle(sketch, "E46.0", {"center": v(0, 0) * mm, "radius": 5 * mm});
            skLineSegment(sketch, "E47", {"start": v(3, 4) * mm, "end": v(1.5, 50) * mm});
            skLineSegment(sketch, "E48", {"start": v(1.5, 50) * mm, "end": v(0, 50) * mm});
            skLineSegment(sketch, "E49.MirrorCS", {"start": v(-1.5, 50) * mm, "end": v(0, 50) * mm});
            skLineSegment(sketch, "E50.MirrorCS", {"start": v(-3, 4) * mm, "end": v(-1.5, 50) * mm});
            skSolve(sketch);
        }
        {
            var Q0;
            Q0 = qSketchRegion(id + "F33", true);
            extrude(context, id + "F34", {"entities" : qUnion([Q0]), "operationType" : NewBodyOperationType.ADD, "depth" : 1 * mm, "offsetDistance" : 25 * mm});
        }
        {
            var Q0;
            Q0=makeQuery(id+"F6.opExtrude","CAP_FACE",FACE,{"disambiguationData":[OSD([sQuery(id+"F4.wireOp",EDGE,"E1")])],"isStart":false});
            var sketch = newSketch(context, id + "F35", { "sketchPlane" : qUnion([Q0])});
            skCircle(sketch, "E51", {"center": v(0, 0) * mm, "radius": 5 * mm});
            skLineSegment(sketch, "E52", {"start": v(2, 4.58) * mm, "end": v(0.5, 80) * mm});
            skLineSegment(sketch, "E53", {"start": v(0.5, 80) * mm, "end": v(0, 80) * mm});
            skLineSegment(sketch, "E54.MirrorCS", {"start": v(-0.5, 80) * mm, "end": v(0, 80) * mm});
            skLineSegment(sketch, "E55.MirrorCS", {"start": v(-2, 4.58) * mm, "end": v(-0.5, 80) * mm});
            skSolve(sketch);
        }
        {
            var Q0;
            Q0 = qSketchRegion(id + "F35", true);
            extrude(context, id + "F36", {"entities" : qUnion([Q0]), "operationType" : NewBodyOperationType.ADD, "oppositeDirection" : true, "depth" : 1 * mm, "offsetDistance" : 25 * mm});
        }
    });
